FCSTD DOCUMENT  (FreeCAD 0.21R33771 (Git))
Label: RING3
License: All rights reserved
LicenseURL: http://en.wikipedia.org/wiki/All_rights_reserved
objects: Part::Part2DObjectPython×252, App::FeaturePython×24, App::DocumentObjectGroup×1
note: 252 computed .brp shape members not serialized (recipe doc carries the construction recipe); baked Part::Feature solids carry a one-line shape summary decoded from their .brp

FEATURE [Part::Part2DObjectPython] Rectangle  # Draft 2D object (typed FeaturePython)
  Area = 0
  ChamferSize = 0
  Columns = 1
  FilletRadius = 0
  Height = 6
  Length = 6
  MakeFace = false
  Placement = pos=(269.144,-43.1167,0) rot=(0,0,1;4.70122rad)
  Rows = 1
FEATURE [App::FeaturePython] Text  # WARN: FeaturePython — macro-defined, semantics opaque (R4)
  Placement = pos=(270.79,-53.3517,0) rot=(0,0,-1;4.73892rad)
  Text = 2
FEATURE [App::FeaturePython] Text001  # WARN: FeaturePython — macro-defined, semantics opaque (R4)
  Placement = pos=(268.047,49.5386,0) rot=(0,0,1;2.6241rad)
  Text = 6.
FEATURE [Part::Part2DObjectPython] Line  # Draft 2D object (typed FeaturePython)
  Area = 0
  ChamferSize = 0
  Closed = false
  End = (271.44,-106.146,0)
  FilletRadius = 0
  Length = 60
  MakeFace = true
  Placement = pos=(321.297,225.428,0) rot=(0,0,1;4.70122rad)
  Points = (2) [(272.11,-46.15,0),(332.11,-46.15,0)]
  Start = (272.11,-46.15,0)
  Subdivisions = 0
FEATURE [Part::Part2DObjectPython] Circle  # Draft 2D object (typed FeaturePython)
  Area = 1.13097
  FirstAngle = 0
  LastAngle = 0
  MakeFace = true
  Placement = pos=(272.07,-49.7498,0) rot=(0,0,1;4.70122rad)
  Radius = 0.6
FEATURE [Part::Part2DObjectPython] Rectangle001  # Draft 2D object (typed FeaturePython)
  Area = 0
  ChamferSize = 0
  Columns = 1
  FilletRadius = 0
  Height = 6
  Length = 6
  MakeFace = false
  Placement = pos=(270.385,-29.144,0) rot=(0,0,1;5.08397rad)
  Rows = 1
FEATURE [Part::Part2DObjectPython] Line001  # Draft 2D object (typed FeaturePython)
  Area = 0
  ChamferSize = 0
  Closed = false
  End = (296.055,-86.7553,0)
  FilletRadius = 0
  Length = 60
  MakeFace = true
  Placement = pos=(203.43,235.904,0) rot=(0,0,1;5.08397rad)
  Points = (2) [(274.27,-30.85,0),(334.27,-30.85,0)]
  Start = (274.27,-30.85,0)
  Subdivisions = 0
FEATURE [Part::Part2DObjectPython] Circle001  # Draft 2D object (typed FeaturePython)
  Area = 1.13097
  FirstAngle = 0
  LastAngle = 0
  MakeFace = true
  Placement = pos=(275.577,-34.2043,0) rot=(0,0,1;5.08397rad)
  Radius = 0.6
FEATURE [Part::Part2DObjectPython] Rectangle002  # Draft 2D object (typed FeaturePython)
  Area = 0
  ChamferSize = 0
  Columns = 1
  FilletRadius = 0
  Height = 6
  Length = 6
  MakeFace = false
  Placement = pos=(271.331,-15.2783,0) rot=(0,0,1;5.4573rad)
  Rows = 1
FEATURE [Part::Part2DObjectPython] Line002  # Draft 2D object (typed FeaturePython)
  Area = 0
  ChamferSize = 0
  Closed = false
  End = (316.244,-59.5591,0)
  FilletRadius = 0
  Length = 60
  MakeFace = true
  Placement = pos=(100.118,197.609,0) rot=(0,0,1;5.4573rad)
  Points = (2) [(275.57,-15.45,0),(335.57,-15.45,0)]
  Start = (275.57,-15.45,0)
  Subdivisions = 0
FEATURE [Part::Part2DObjectPython] Circle002  # Draft 2D object (typed FeaturePython)
  Area = 1.13097
  FirstAngle = 0
  LastAngle = 0
  MakeFace = true
  Placement = pos=(278.01,-18.0965,0) rot=(0,0,1;5.4573rad)
  Radius = 0.6
FEATURE [Part::Part2DObjectPython] Rectangle003  # Draft 2D object (typed FeaturePython)
  Area = 0
  ChamferSize = 0
  Columns = 1
  FilletRadius = 0
  Height = 6
  Length = 6
  MakeFace = false
  Placement = pos=(271.89,-1.0508,0) rot=(0,0,1;5.74807rad)
  Rows = 1
FEATURE [Part::Part2DObjectPython] Line003  # Draft 2D object (typed FeaturePython)
  Area = 0
  ChamferSize = 0
  Closed = false
  End = (327.613,-30.5966,0)
  FilletRadius = 0
  Length = 60
  MakeFace = true
  Placement = pos=(38.5825,140.744,0) rot=(0,0,1;5.74807rad)
  Points = (2) [(276,0,0),(336,0,0)]
  Start = (276,-5.68e-14,0)
  Subdivisions = 0
FEATURE [Part::Part2DObjectPython] Circle003  # Draft 2D object (typed FeaturePython)
  Area = 1.13097
  FirstAngle = 0
  LastAngle = 0
  MakeFace = true
  Placement = pos=(279.097,-1.83579,0) rot=(0,0,1;5.74807rad)
  Radius = 0.6
FEATURE [Part::Part2DObjectPython] Rectangle004  # Draft 2D object (typed FeaturePython)
  Area = 0
  ChamferSize = 0
  Columns = 1
  FilletRadius = 0
  Height = 6
  Length = 6
  MakeFace = false
  Placement = pos=(271.77,13.5629,0) rot=(0,0,1;5.95873rad)
  Rows = 1
FEATURE [Part::Part2DObjectPython] Line004  # Draft 2D object (typed FeaturePython)
  Area = 0
  ChamferSize = 0
  Closed = false
  End = (332.439,-3.67763,0)
  FilletRadius = 0
  Length = 60
  MakeFace = true
  Placement = pos=(9.45276,88.6561,0) rot=(0,0,1;5.95873rad)
  Points = (2) [(275.57,15.45,0),(335.57,15.45,0)]
  Start = (275.57,15.45,0)
  Subdivisions = 0
FEATURE [Part::Part2DObjectPython] Circle004  # Draft 2D object (typed FeaturePython)
  Area = 1.13097
  FirstAngle = 0
  LastAngle = 0
  MakeFace = true
  Placement = pos=(278.982,14.3023,0) rot=(0,0,1;5.95873rad)
  Radius = 0.6
FEATURE [Part::Part2DObjectPython] Rectangle005  # Draft 2D object (typed FeaturePython)
  Area = 0
  ChamferSize = 0
  Columns = 1
  FilletRadius = 0
  Height = 6
  Length = 6
  MakeFace = false
  Placement = pos=(270.817,28.3851,0) rot=(0,0,1;6.11773rad)
  Rows = 1
FEATURE [Part::Part2DObjectPython] Line005  # Draft 2D object (typed FeaturePython)
  Area = 0
  ChamferSize = 0
  Closed = false
  End = (333.451,20.9678,0)
  FilletRadius = 0
  Length = 60
  MakeFace = true
  Placement = pos=(-1.33543,45.5945,0) rot=(0,0,1;6.11773rad)
  Points = (2) [(274.27,30.85,0),(334.27,30.85,0)]
  Start = (274.27,30.85,0)
  Subdivisions = 0
FEATURE [Part::Part2DObjectPython] Circle005  # Draft 2D object (typed FeaturePython)
  Area = 1.13097
  FirstAngle = 0
  LastAngle = 0
  MakeFace = true
  Placement = pos=(277.821,30.2571,0) rot=(0,0,1;6.11773rad)
  Radius = 0.6
FEATURE [Part::Part2DObjectPython] Rectangle006  # Draft 2D object (typed FeaturePython)
  Area = 0
  ChamferSize = 0
  Columns = 1
  FilletRadius = 0
  Height = 6
  Length = 6
  MakeFace = false
  Placement = pos=(268.997,43.2674,0) rot=(0,0,1;6.24479rad)
  Rows = 1
FEATURE [Part::Part2DObjectPython] Line006  # Draft 2D object (typed FeaturePython)
  Area = 0
  ChamferSize = 0
  Closed = false
  End = (332.066,43.8467,0)
  FilletRadius = 0
  Length = 60
  MakeFace = true
  Placement = pos=(-1.57103,10.4797,0) rot=(0,0,1;6.24479rad)
  Points = (2) [(272.11,46.15,0),(332.11,46.15,0)]
  Start = (272.11,46.15,0)
  Subdivisions = 0
FEATURE [Part::Part2DObjectPython] Circle006  # Draft 2D object (typed FeaturePython)
  Area = 1.13097
  FirstAngle = 0
  LastAngle = 0
  MakeFace = true
  Placement = pos=(275.707,46.0118,0) rot=(0,0,1;6.24479rad)
  Radius = 0.6
FEATURE [Part::Part2DObjectPython] Rectangle007  # Draft 2D object (typed FeaturePython)
  Area = 0
  ChamferSize = 0
  Columns = 1
  FilletRadius = 0
  Height = 6
  Length = 6
  MakeFace = false
  Placement = pos=(256.356,92.5739,0) rot=(0,0,1;0.191463rad)
  Rows = 1
FEATURE [App::FeaturePython] Text002  # WARN: FeaturePython — macro-defined, semantics opaque (R4)
  Placement = pos=(261.188,89.1931,0) rot=(0,0,-1;4.21532rad)
  Text = 2
FEATURE [App::FeaturePython] Text003  # WARN: FeaturePython — macro-defined, semantics opaque (R4)
  Placement = pos=(207.363,176.926,0) rot=(0,0,1;3.1477rad)
  Text = 7
FEATURE [Part::Part2DObjectPython] Line007  # Draft 2D object (typed FeaturePython)
  Area = 0
  ChamferSize = 0
  Closed = false
  End = (317.634,107.508,0)
  FilletRadius = 0
  Length = 60
  MakeFace = true
  Placement = pos=(23.0132,-47.4792,0) rot=(0,0,1;0.191463rad)
  Points = (2) [(258.73,96.09,0),(318.73,96.09,0)]
  Start = (258.73,96.09,0)
  Subdivisions = 0
FEATURE [Part::Part2DObjectPython] Circle007  # Draft 2D object (typed FeaturePython)
  Area = 1.13097
  FirstAngle = 0
  LastAngle = 0
  MakeFace = true
  Placement = pos=(262.264,96.7751,0) rot=(0,0,1;0.191463rad)
  Radius = 0.6
FEATURE [Part::Part2DObjectPython] Rectangle008  # Draft 2D object (typed FeaturePython)
  Area = 0
  ChamferSize = 0
  Columns = 1
  FilletRadius = 0
  Height = 6
  Length = 6
  MakeFace = false
  Placement = pos=(250.416,107.017,0) rot=(0,0,1;0.145211rad)
  Rows = 1
FEATURE [Part::Part2DObjectPython] Line008  # Draft 2D object (typed FeaturePython)
  Area = 0
  ChamferSize = 0
  Closed = false
  End = (312.319,119.102,0)
  FilletRadius = 0
  Length = 60
  MakeFace = true
  Placement = pos=(18.6402,-35.4401,0) rot=(0,0,1;0.145211rad)
  Points = (2) [(252.95,110.42,0),(312.95,110.42,0)]
  Start = (252.95,110.42,0)
  Subdivisions = 0
FEATURE [Part::Part2DObjectPython] Circle008  # Draft 2D object (typed FeaturePython)
  Area = 1.13097
  FirstAngle = 0
  LastAngle = 0
  MakeFace = true
  Placement = pos=(256.512,110.941,0) rot=(0,0,1;0.145211rad)
  Radius = 0.6
FEATURE [Part::Part2DObjectPython] Rectangle009  # Draft 2D object (typed FeaturePython)
  Area = 0
  ChamferSize = 0
  Columns = 1
  FilletRadius = 0
  Height = 6
  Length = 6
  MakeFace = false
  Placement = pos=(243.301,121.481,0) rot=(0,0,1;6.2598rad)
  Rows = 1
FEATURE [Part::Part2DObjectPython] Line009  # Draft 2D object (typed FeaturePython)
  Area = 0
  ChamferSize = 0
  Closed = false
  End = (306.354,123.007,0)
  FilletRadius = 0
  Length = 60
  MakeFace = true
  Placement = pos=(-2.84199,5.79545,0) rot=(0,0,1;6.2598rad)
  Points = (2) [(246.37,124.41,0),(306.37,124.41,0)]
  Start = (246.37,124.41,0)
  Subdivisions = 0
FEATURE [Part::Part2DObjectPython] Circle009  # Draft 2D object (typed FeaturePython)
  Area = 1.13097
  FirstAngle = 0
  LastAngle = 0
  MakeFace = true
  Placement = pos=(249.969,124.326,0) rot=(0,0,1;6.2598rad)
  Radius = 0.6
FEATURE [Part::Part2DObjectPython] Rectangle010  # Draft 2D object (typed FeaturePython)
  Area = 0
  ChamferSize = 0
  Columns = 1
  FilletRadius = 0
  Height = 6
  Length = 6
  MakeFace = false
  Placement = pos=(235.214,136.126,0) rot=(0,0,1;5.95541rad)
  Rows = 1
FEATURE [Part::Part2DObjectPython] Line010  # Draft 2D object (typed FeaturePython)
  Area = 0
  ChamferSize = 0
  Closed = false
  End = (295.826,118.684,0)
  FilletRadius = 0
  Length = 60
  MakeFace = true
  Placement = pos=(-31.702,84.2958,0) rot=(0,0,1;5.95541rad)
  Points = (2) [(239.02,138,0),(299.02,138,0)]
  Start = (239.02,138,0)
  Subdivisions = 0
FEATURE [Part::Part2DObjectPython] Circle010  # Draft 2D object (typed FeaturePython)
  Area = 1.13097
  FirstAngle = 0
  LastAngle = 0
  MakeFace = true
  Placement = pos=(242.428,136.841,0) rot=(0,0,1;5.95541rad)
  Radius = 0.6
FEATURE [Part::Part2DObjectPython] Rectangle011  # Draft 2D object (typed FeaturePython)
  Area = 0
  ChamferSize = 0
  Columns = 1
  FilletRadius = 0
  Height = 6
  Length = 6
  MakeFace = false
  Placement = pos=(226.732,150.48,0) rot=(0,0,1;5.65871rad)
  Rows = 1
FEATURE [Part::Part2DObjectPython] Line011  # Draft 2D object (typed FeaturePython)
  Area = 0
  ChamferSize = 0
  Closed = false
  End = (279.596,116.08,0)
  FilletRadius = 0
  Length = 60
  MakeFace = true
  Placement = pos=(-44.7974,163.542,0) rot=(0,0,1;5.65871rad)
  Points = (2) [(230.92,151.16,0),(290.92,151.16,0)]
  Start = (230.92,151.16,0)
  Subdivisions = 0
FEATURE [Part::Part2DObjectPython] Circle011  # Draft 2D object (typed FeaturePython)
  Area = 1.13097
  FirstAngle = 0
  LastAngle = 0
  MakeFace = true
  Placement = pos=(233.841,149.055,0) rot=(0,0,1;5.65871rad)
  Radius = 0.6
FEATURE [Part::Part2DObjectPython] Rectangle012  # Draft 2D object (typed FeaturePython)
  Area = 0
  ChamferSize = 0
  Columns = 1
  FilletRadius = 0
  Height = 6
  Length = 6
  MakeFace = false
  Placement = pos=(217.857,163.826,0) rot=(0,0,1;5.50337rad)
  Rows = 1
FEATURE [Part::Part2DObjectPython] Line012  # Draft 2D object (typed FeaturePython)
  Area = 0
  ChamferSize = 0
  Closed = false
  End = (264.763,121.661,0)
  FilletRadius = 0
  Length = 60
  MakeFace = true
  Placement = pos=(-51.0336,203.514,0) rot=(0,0,1;5.50337rad)
  Points = (2) [(222.1,163.85,0),(282.1,163.85,0)]
  Start = (222.1,163.85,0)
  Subdivisions = 0
FEATURE [Part::Part2DObjectPython] Circle012  # Draft 2D object (typed FeaturePython)
  Area = 1.13097
  FirstAngle = 0
  LastAngle = 0
  MakeFace = true
  Placement = pos=(224.66,161.319,0) rot=(0,0,1;5.50337rad)
  Radius = 0.6
FEATURE [Part::Part2DObjectPython] Rectangle013  # Draft 2D object (typed FeaturePython)
  Area = 0
  ChamferSize = 0
  Columns = 1
  FilletRadius = 0
  Height = 6
  Length = 6
  MakeFace = false
  Placement = pos=(208.339,176.143,0) rot=(0,0,1;5.46882rad)
  Rows = 1
FEATURE [Part::Part2DObjectPython] Line013  # Draft 2D object (typed FeaturePython)
  Area = 0
  ChamferSize = 0
  Closed = false
  End = (253.76,132.382,0)
  FilletRadius = 0
  Length = 60
  MakeFace = true
  Placement = pos=(-61.3375,209.821,0) rot=(0,0,1;5.46882rad)
  Points = (2) [(212.58,176.02,0),(272.58,176.02,0)]
  Start = (212.58,176.02,0)
  Subdivisions = 0
FEATURE [Part::Part2DObjectPython] Circle013  # Draft 2D object (typed FeaturePython)
  Area = 1.13097
  FirstAngle = 0
  LastAngle = 0
  MakeFace = true
  Placement = pos=(215.051,173.402,0) rot=(0,0,1;5.46882rad)
  Radius = 0.6
FEATURE [Part::Part2DObjectPython] Rectangle014  # Draft 2D object (typed FeaturePython)
  Area = 0
  ChamferSize = 0
  Columns = 1
  FilletRadius = 0
  Height = 6
  Length = 6
  MakeFace = false
  Placement = pos=(171.868,211.706,0) rot=(0,0,1;5.70531rad)
  Rows = 1
FEATURE [App::FeaturePython] Text004  # WARN: FeaturePython — macro-defined, semantics opaque (R4)
  Placement = pos=(181.597,207.836,0) rot=(0,0,-1;3.69172rad)
  Text = 2
FEATURE [App::FeaturePython] Text005  # WARN: FeaturePython — macro-defined, semantics opaque (R4)
  Placement = pos=(91.1209,256.902,0) rot=(0,0,1;3.6713rad)
  Text = 8
FEATURE [Part::Part2DObjectPython] Line014  # Draft 2D object (typed FeaturePython)
  Area = 0
  ChamferSize = 0
  Closed = false
  End = (226.277,179.805,0)
  FilletRadius = 0
  Length = 60
  MakeFace = true
  Placement = pos=(-87.5399,130.669,0) rot=(0,0,1;5.70531rad)
  Points = (2) [(176.02,212.58,0),(236.02,212.58,0)]
  Start = (176.02,212.58,0)
  Subdivisions = 0
FEATURE [Part::Part2DObjectPython] Circle014  # Draft 2D object (typed FeaturePython)
  Area = 1.13097
  FirstAngle = 0
  LastAngle = 0
  MakeFace = true
  Placement = pos=(179.035,210.614,0) rot=(0,0,1;5.70531rad)
  Radius = 0.6
FEATURE [Part::Part2DObjectPython] Rectangle015  # Draft 2D object (typed FeaturePython)
  Area = 0
  ChamferSize = 0
  Columns = 1
  FilletRadius = 0
  Height = 6
  Length = 6
  MakeFace = false
  Placement = pos=(159.811,220.802,0) rot=(0,0,1;5.80863rad)
  Rows = 1
FEATURE [Part::Part2DObjectPython] Line015  # Draft 2D object (typed FeaturePython)
  Area = 0
  ChamferSize = 0
  Closed = false
  End = (217.22,194.683,0)
  FilletRadius = 0
  Length = 60
  MakeFace = true
  Placement = pos=(-83.3809,99.413,0) rot=(0,0,1;5.80863rad)
  Points = (2) [(163.85,222.1,0),(223.85,222.1,0)]
  Start = (163.85,222.1,0)
  Subdivisions = 0
FEATURE [Part::Part2DObjectPython] Circle015  # Draft 2D object (typed FeaturePython)
  Area = 1.13097
  FirstAngle = 0
  LastAngle = 0
  MakeFace = true
  Placement = pos=(167.052,220.455,0) rot=(0,0,1;5.80863rad)
  Radius = 0.6
FEATURE [Part::Part2DObjectPython] Rectangle016  # Draft 2D object (typed FeaturePython)
  Area = 0
  ChamferSize = 0
  Columns = 1
  FilletRadius = 0
  Height = 6
  Length = 6
  MakeFace = false
  Placement = pos=(147.277,229.211,0) rot=(0,0,1;5.91248rad)
  Rows = 1
FEATURE [Part::Part2DObjectPython] Line016  # Draft 2D object (typed FeaturePython)
  Area = 0
  ChamferSize = 0
  Closed = false
  End = (207.084,209.183,0)
  FilletRadius = 0
  Length = 60
  MakeFace = true
  Placement = pos=(-73.3885,70.4477,0) rot=(0,0,1;5.91248rad)
  Points = (2) [(151.16,230.92,0),(211.16,230.92,0)]
  Start = (151.16,230.92,0)
  Subdivisions = 0
FEATURE [Part::Part2DObjectPython] Circle016  # Draft 2D object (typed FeaturePython)
  Area = 1.13097
  FirstAngle = 0
  LastAngle = 0
  MakeFace = true
  Placement = pos=(154.515,229.616,0) rot=(0,0,1;5.91248rad)
  Radius = 0.6
FEATURE [Part::Part2DObjectPython] Rectangle017  # Draft 2D object (typed FeaturePython)
  Area = 0
  ChamferSize = 0
  Columns = 1
  FilletRadius = 0
  Height = 6
  Length = 6
  MakeFace = false
  Placement = pos=(134.314,236.919,0) rot=(0,0,1;6.0158rad)
  Rows = 1
FEATURE [Part::Part2DObjectPython] Line017  # Draft 2D object (typed FeaturePython)
  Area = 0
  ChamferSize = 0
  Closed = false
  End = (195.868,223.167,0)
  FilletRadius = 0
  Length = 60
  MakeFace = true
  Placement = pos=(-58.2476,44.9545,0) rot=(0,0,1;6.0158rad)
  Points = (2) [(138,239.02,0),(198,239.02,0)]
  Start = (138,239.02,0)
  Subdivisions = 0
FEATURE [Part::Part2DObjectPython] Circle017  # Draft 2D object (typed FeaturePython)
  Area = 1.13097
  FirstAngle = 0
  LastAngle = 0
  MakeFace = true
  Placement = pos=(141.472,238.069,0) rot=(0,0,1;6.0158rad)
  Radius = 0.6
FEATURE [Part::Part2DObjectPython] Rectangle018  # Draft 2D object (typed FeaturePython)
  Area = 0
  ChamferSize = 0
  Columns = 1
  FilletRadius = 0
  Height = 6
  Length = 6
  MakeFace = false
  Placement = pos=(120.961,243.9,0) rot=(0,0,1;6.1193rad)
  Rows = 1
FEATURE [Part::Part2DObjectPython] Line018  # Draft 2D object (typed FeaturePython)
  Area = 0
  ChamferSize = 0
  Closed = false
  End = (183.606,236.581,0)
  FilletRadius = 0
  Length = 60
  MakeFace = true
  Placement = pos=(-38.5292,23.5992,0) rot=(0,0,1;6.1193rad)
  Points = (2) [(124.41,246.37,0),(184.41,246.37,0)]
  Start = (124.41,246.37,0)
  Subdivisions = 0
FEATURE [Part::Part2DObjectPython] Circle018  # Draft 2D object (typed FeaturePython)
  Area = 1.13097
  FirstAngle = 0
  LastAngle = 0
  MakeFace = true
  Placement = pos=(127.962,245.783,0) rot=(0,0,1;6.1193rad)
  Radius = 0.6
FEATURE [Part::Part2DObjectPython] Rectangle019  # Draft 2D object (typed FeaturePython)
  Area = 0
  ChamferSize = 0
  Columns = 1
  FilletRadius = 0
  Height = 6
  Length = 6
  MakeFace = false
  Placement = pos=(107.269,250.109,0) rot=(0,0,1;6.23152rad)
  Rows = 1
FEATURE [Part::Part2DObjectPython] Line019  # Draft 2D object (typed FeaturePython)
  Area = 0
  ChamferSize = 0
  Closed = false
  End = (170.34,249.852,0)
  FilletRadius = 0
  Length = 60
  MakeFace = true
  Placement = pos=(-12.9147,6.03943,0) rot=(0,0,1;6.23152rad)
  Points = (2) [(110.42,252.95,0),(170.42,252.95,0)]
  Start = (110.42,252.95,0)
  Subdivisions = 0
FEATURE [Part::Part2DObjectPython] Circle019  # Draft 2D object (typed FeaturePython)
  Area = 1.13097
  FirstAngle = 0
  LastAngle = 0
  MakeFace = true
  Placement = pos=(114.015,252.764,0) rot=(0,0,1;6.23152rad)
  Radius = 0.6
FEATURE [Part::Part2DObjectPython] Rectangle020  # Draft 2D object (typed FeaturePython)
  Area = 0
  ChamferSize = 0
  Columns = 1
  FilletRadius = 0
  Height = 6
  Length = 6
  MakeFace = false
  Placement = pos=(93.3516,255.489,0) rot=(0,0,1;0.083776rad)
  Rows = 1
FEATURE [Part::Part2DObjectPython] Line020  # Draft 2D object (typed FeaturePython)
  Area = 0
  ChamferSize = 0
  Closed = false
  End = (155.88,263.751,0)
  FilletRadius = 0
  Length = 60
  MakeFace = true
  Placement = pos=(21.987,-7.1332,0) rot=(0,0,1;0.083776rad)
  Points = (2) [(96.09,258.73,0),(156.09,258.73,0)]
  Start = (96.09,258.73,0)
  Subdivisions = 0
FEATURE [Part::Part2DObjectPython] Circle020  # Draft 2D object (typed FeaturePython)
  Area = 1.13097
  FirstAngle = 0
  LastAngle = 0
  MakeFace = true
  Placement = pos=(99.6774,259.031,0) rot=(0,0,1;0.083776rad)
  Radius = 0.6
FEATURE [Part::Part2DObjectPython] Rectangle021  # Draft 2D object (typed FeaturePython)
  Area = 0
  ChamferSize = 0
  Columns = 1
  FilletRadius = 0
  Height = 6
  Length = 6
  MakeFace = false
  Placement = pos=(48.0649,268.324,0) rot=(0,0,1;1.25367rad)
  Rows = 1
FEATURE [App::FeaturePython] Text006  # WARN: FeaturePython — macro-defined, semantics opaque (R4)
  Placement = pos=(53.3517,270.79,0) rot=(0,0,-1;3.16812rad)
  Text = 2
FEATURE [App::FeaturePython] Text007  # WARN: FeaturePython — macro-defined, semantics opaque (R4)
  Placement = pos=(-49.5386,268.047,0) rot=(0,0,1;4.1949rad)
  Text = 9
FEATURE [Part::Part2DObjectPython] Line021  # Draft 2D object (typed FeaturePython)
  Area = 0
  ChamferSize = 0
  Closed = false
  End = (64.8602,329.118,0)
  FilletRadius = 0
  Length = 60
  MakeFace = true
  Placement = pos=(290.3,143.407,0) rot=(0,0,1;1.25367rad)
  Points = (2) [(46.15,272.11,0),(106.15,272.11,0)]
  Start = (46.15,272.11,0)
  Subdivisions = 0
FEATURE [Part::Part2DObjectPython] Circle021  # Draft 2D object (typed FeaturePython)
  Area = 1.13097
  FirstAngle = 0
  LastAngle = 0
  MakeFace = true
  Placement = pos=(47.2726,275.53,0) rot=(0,0,1;1.25367rad)
  Radius = 0.6
FEATURE [Part::Part2DObjectPython] Rectangle022  # Draft 2D object (typed FeaturePython)
  Area = 0
  ChamferSize = 0
  Columns = 1
  FilletRadius = 0
  Height = 6
  Length = 6
  MakeFace = false
  Placement = pos=(34.7405,272.578,0) rot=(0,0,1;1.94587rad)
  Rows = 1
FEATURE [Part::Part2DObjectPython] Line022  # Draft 2D object (typed FeaturePython)
  Area = 0
  ChamferSize = 0
  Closed = false
  End = (8.86967,330.099,0)
  FilletRadius = 0
  Length = 60
  MakeFace = true
  Placement = pos=(297.355,346.04,0) rot=(0,0,1;1.94587rad)
  Points = (2) [(30.85,274.27,0),(90.85,274.27,0)]
  Start = (30.85,274.27,0)
  Subdivisions = 0
FEATURE [Part::Part2DObjectPython] Circle022  # Draft 2D object (typed FeaturePython)
  Area = 1.13097
  FirstAngle = 0
  LastAngle = 0
  MakeFace = true
  Placement = pos=(29.5312,277.62,0) rot=(0,0,1;1.94587rad)
  Radius = 0.6
FEATURE [Part::Part2DObjectPython] Rectangle023  # Draft 2D object (typed FeaturePython)
  Area = 0
  ChamferSize = 0
  Columns = 1
  FilletRadius = 0
  Height = 6
  Length = 6
  MakeFace = false
  Placement = pos=(19.6498,276.171,0) rot=(0,0,1;2.49844rad)
  Rows = 1
FEATURE [Part::Part2DObjectPython] Line023  # Draft 2D object (typed FeaturePython)
  Area = 0
  ChamferSize = 0
  Closed = false
  End = (-32.5625,311.553,0)
  FilletRadius = 0
  Length = 60
  MakeFace = true
  Placement = pos=(193.079,486.818,0) rot=(0,0,1;2.49844rad)
  Points = (2) [(15.45,275.57,0),(75.45,275.57,0)]
  Start = (15.45,275.57,0)
  Subdivisions = 0
FEATURE [Part::Part2DObjectPython] Circle023  # Draft 2D object (typed FeaturePython)
  Area = 1.13097
  FirstAngle = 0
  LastAngle = 0
  MakeFace = true
  Placement = pos=(12.5693,277.729,0) rot=(0,0,1;2.49844rad)
  Radius = 0.6
FEATURE [Part::Part2DObjectPython] Rectangle024  # Draft 2D object (typed FeaturePython)
  Area = 0
  ChamferSize = 0
  Columns = 1
  FilletRadius = 0
  Height = 6
  Length = 6
  MakeFace = false
  Placement = pos=(3.67238,278.125,0) rot=(0,0,1;2.88067rad)
  Rows = 1
FEATURE [Part::Part2DObjectPython] Line024  # Draft 2D object (typed FeaturePython)
  Area = 0
  ChamferSize = 0
  Closed = false
  End = (-57.9691,291.479,0)
  FilletRadius = 0
  Length = 60
  MakeFace = true
  Placement = pos=(71.2014,542.658,0) rot=(0,0,1;2.88067rad)
  Points = (2) [(0,276,0),(60,276,0)]
  Start = (0,276,0)
  Subdivisions = 0
FEATURE [Part::Part2DObjectPython] Circle024  # Draft 2D object (typed FeaturePython)
  Area = 1.13097
  FirstAngle = 0
  LastAngle = 0
  MakeFace = true
  Placement = pos=(-3.47814,276.929,0) rot=(0,0,1;2.88067rad)
  Radius = 0.6
FEATURE [Part::Part2DObjectPython] Rectangle025  # Draft 2D object (typed FeaturePython)
  Area = 0
  ChamferSize = 0
  Columns = 1
  FilletRadius = 0
  Height = 6
  Length = 6
  MakeFace = false
  Placement = pos=(-12.4484,278.568,0) rot=(0,0,1;3.14107rad)
  Rows = 1
FEATURE [Part::Part2DObjectPython] Line025  # Draft 2D object (typed FeaturePython)
  Area = 0
  ChamferSize = 0
  Closed = false
  End = (-75.45,275.601,0)
  FilletRadius = 0
  Length = 60
  MakeFace = true
  Placement = pos=(-30.7557,551.148,0) rot=(0,0,1;3.14107rad)
  Points = (2) [(-15.45,275.57,0),(44.55,275.57,0)]
  Start = (-15.45,275.57,0)
  Subdivisions = 0
FEATURE [Part::Part2DObjectPython] Circle025  # Draft 2D object (typed FeaturePython)
  Area = 1.13097
  FirstAngle = 0
  LastAngle = 0
  MakeFace = true
  Placement = pos=(-19.05,275.572,0) rot=(0,0,1;3.14107rad)
  Radius = 0.6
FEATURE [Part::Part2DObjectPython] Rectangle026  # Draft 2D object (typed FeaturePython)
  Area = 0
  ChamferSize = 0
  Columns = 1
  FilletRadius = 0
  Height = 6
  Length = 6
  MakeFace = false
  Placement = pos=(-27.849,277.269,0) rot=(0,0,1;3.14124rad)
  Rows = 1
FEATURE [Part::Part2DObjectPython] Line026  # Draft 2D object (typed FeaturePython)
  Area = 0
  ChamferSize = 0
  Closed = false
  End = (-90.85,274.291,0)
  FilletRadius = 0
  Length = 60
  MakeFace = true
  Placement = pos=(-61.6043,548.551,0) rot=(0,0,1;3.14124rad)
  Points = (2) [(-30.85,274.27,0),(29.15,274.27,0)]
  Start = (-30.85,274.27,0)
  Subdivisions = 0
FEATURE [Part::Part2DObjectPython] Circle026  # Draft 2D object (typed FeaturePython)
  Area = 1.13097
  FirstAngle = 0
  LastAngle = 0
  MakeFace = true
  Placement = pos=(-34.45,274.271,0) rot=(0,0,1;3.14124rad)
  Radius = 0.6
FEATURE [Part::Part2DObjectPython] Rectangle027  # Draft 2D object (typed FeaturePython)
  Area = 0
  ChamferSize = 0
  Columns = 1
  FilletRadius = 0
  Height = 6
  Length = 6
  MakeFace = false
  Placement = pos=(-43.15,275.11,0) rot=(0,0,1;3.14159rad)
  Rows = 1
FEATURE [Part::Part2DObjectPython] Line027  # Draft 2D object (typed FeaturePython)
  Area = 0
  ChamferSize = 0
  Closed = false
  End = (-106.15,272.11,0)
  FilletRadius = 0
  Length = 60
  MakeFace = true
  Placement = pos=(-92.3,544.22,0) rot=(0,0,1;3.14159rad)
  Points = (2) [(-46.15,272.11,0),(13.85,272.11,0)]
  Start = (-46.15,272.11,0)
  Subdivisions = 0
FEATURE [Part::Part2DObjectPython] Circle027  # Draft 2D object (typed FeaturePython)
  Area = 1.13097
  FirstAngle = 0
  LastAngle = 0
  MakeFace = true
  Placement = pos=(-49.75,272.11,0) rot=(0,0,1;3.14159rad)
  Radius = 0.6
FEATURE [Part::Part2DObjectPython] Rectangle028  # Draft 2D object (typed FeaturePython)
  Area = 0
  ChamferSize = 0
  Columns = 1
  FilletRadius = 0
  Height = 6
  Length = 6
  MakeFace = false
  Placement = pos=(-93.09,261.73,0) rot=(0,0,1;3.14159rad)
  Rows = 1
FEATURE [App::FeaturePython] Text008  # WARN: FeaturePython — macro-defined, semantics opaque (R4)
  Placement = pos=(-89.1931,261.188,0) rot=(0,0,-1;2.64452rad)
  Text = 2
FEATURE [App::FeaturePython] Text009  # WARN: FeaturePython — macro-defined, semantics opaque (R4)
  Placement = pos=(-176.926,207.363,0) rot=(0,0,1;4.7185rad)
  Text = 10
FEATURE [Part::Part2DObjectPython] Line028  # Draft 2D object (typed FeaturePython)
  Area = 0
  ChamferSize = 0
  Closed = false
  End = (-156.09,258.73,0)
  FilletRadius = 0
  Length = 60
  MakeFace = true
  Placement = pos=(-192.18,517.46,0) rot=(0,0,1;3.14159rad)
  Points = (2) [(-96.09,258.73,0),(-36.09,258.73,0)]
  Start = (-96.09,258.73,0)
  Subdivisions = 0
FEATURE [Part::Part2DObjectPython] Circle028  # Draft 2D object (typed FeaturePython)
  Area = 1.13097
  FirstAngle = 0
  LastAngle = 0
  MakeFace = true
  Placement = pos=(-99.69,258.73,0) rot=(0,0,1;3.14159rad)
  Radius = 0.6
FEATURE [Part::Part2DObjectPython] Rectangle029  # Draft 2D object (typed FeaturePython)
  Area = 0
  ChamferSize = 0
  Columns = 1
  FilletRadius = 0
  Height = 6
  Length = 6
  MakeFace = false
  Placement = pos=(-107.42,255.95,0) rot=(0,0,1;3.14159rad)
  Rows = 1
FEATURE [Part::Part2DObjectPython] Line029  # Draft 2D object (typed FeaturePython)
  Area = 0
  ChamferSize = 0
  Closed = false
  End = (-170.42,252.95,0)
  FilletRadius = 0
  Length = 60
  MakeFace = true
  Placement = pos=(-220.84,505.9,0) rot=(0,0,1;3.14159rad)
  Points = (2) [(-110.42,252.95,0),(-50.42,252.95,0)]
  Start = (-110.42,252.95,0)
  Subdivisions = 0
FEATURE [Part::Part2DObjectPython] Circle029  # Draft 2D object (typed FeaturePython)
  Area = 1.13097
  FirstAngle = 0
  LastAngle = 0
  MakeFace = true
  Placement = pos=(-114.02,252.95,0) rot=(0,0,1;3.14159rad)
  Radius = 0.6
FEATURE [Part::Part2DObjectPython] Rectangle030  # Draft 2D object (typed FeaturePython)
  Area = 0
  ChamferSize = 0
  Columns = 1
  FilletRadius = 0
  Height = 6
  Length = 6
  MakeFace = false
  Placement = pos=(-125.426,250.489,0) rot=(0,0,1;4.16889rad)
  Rows = 1
FEATURE [Part::Part2DObjectPython] Line030  # Draft 2D object (typed FeaturePython)
  Area = 0
  ChamferSize = 0
  Closed = false
  End = (-155.438,195.016,0)
  FilletRadius = 0
  Length = 60
  MakeFace = true
  Placement = pos=(-399.616,267.292,0) rot=(0,0,1;4.16889rad)
  Points = (2) [(-124.41,246.37,0),(-64.41,246.37,0)]
  Start = (-124.41,246.37,0)
  Subdivisions = 0
FEATURE [Part::Part2DObjectPython] Circle030  # Draft 2D object (typed FeaturePython)
  Area = 1.13097
  FirstAngle = 0
  LastAngle = 0
  MakeFace = true
  Placement = pos=(-126.272,243.289,0) rot=(0,0,1;4.16889rad)
  Radius = 0.6
FEATURE [Part::Part2DObjectPython] Rectangle031  # Draft 2D object (typed FeaturePython)
  Area = 0
  ChamferSize = 0
  Columns = 1
  FilletRadius = 0
  Height = 6
  Length = 6
  MakeFace = false
  Placement = pos=(-138.447,243.239,0) rot=(0,0,1;4.03258rad)
  Rows = 1
FEATURE [Part::Part2DObjectPython] Line031  # Draft 2D object (typed FeaturePython)
  Area = 0
  ChamferSize = 0
  Closed = false
  End = (-175.719,192.358,0)
  FilletRadius = 0
  Length = 60
  MakeFace = true
  Placement = pos=(-410.637,281.956,0) rot=(0,0,1;4.03258rad)
  Points = (2) [(-138,239.02,0),(-78,239.02,0)]
  Start = (-138,239.02,0)
  Subdivisions = 0
FEATURE [Part::Part2DObjectPython] Circle031  # Draft 2D object (typed FeaturePython)
  Area = 1.13097
  FirstAngle = 0
  LastAngle = 0
  MakeFace = true
  Placement = pos=(-140.263,236.22,0) rot=(0,0,1;4.03258rad)
  Radius = 0.6
FEATURE [Part::Part2DObjectPython] Rectangle032  # Draft 2D object (typed FeaturePython)
  Area = 0
  ChamferSize = 0
  Columns = 1
  FilletRadius = 0
  Height = 6
  Length = 6
  MakeFace = false
  Placement = pos=(-148.16,233.92,0) rot=(0,0,1;3.14159rad)
  Rows = 1
FEATURE [Part::Part2DObjectPython] Line032  # Draft 2D object (typed FeaturePython)
  Area = 0
  ChamferSize = 0
  Closed = false
  End = (-211.16,230.92,0)
  FilletRadius = 0
  Length = 60
  MakeFace = true
  Placement = pos=(-302.32,461.84,0) rot=(0,0,1;3.14159rad)
  Points = (2) [(-151.16,230.92,0),(-91.16,230.92,0)]
  Start = (-151.16,230.92,0)
  Subdivisions = 0
FEATURE [Part::Part2DObjectPython] Circle032  # Draft 2D object (typed FeaturePython)
  Area = 1.13097
  FirstAngle = 0
  LastAngle = 0
  MakeFace = true
  Placement = pos=(-154.76,230.92,0) rot=(0,0,1;3.14159rad)
  Radius = 0.6
FEATURE [Part::Part2DObjectPython] Rectangle033  # Draft 2D object (typed FeaturePython)
  Area = 0
  ChamferSize = 0
  Columns = 1
  FilletRadius = 0
  Height = 6
  Length = 6
  MakeFace = false
  Placement = pos=(-161.861,225.847,0) rot=(0,0,1;3.439rad)
  Rows = 1
FEATURE [Part::Part2DObjectPython] Line033  # Draft 2D object (typed FeaturePython)
  Area = 0
  ChamferSize = 0
  Closed = false
  End = (-221.216,204.518,0)
  FilletRadius = 0
  Length = 60
  MakeFace = true
  Placement = pos=(-385.591,386.435,0) rot=(0,0,1;3.439rad)
  Points = (2) [(-163.85,222.1,0),(-103.85,222.1,0)]
  Start = (-163.85,222.1,0)
  Subdivisions = 0
FEATURE [Part::Part2DObjectPython] Circle033  # Draft 2D object (typed FeaturePython)
  Area = 1.13097
  FirstAngle = 0
  LastAngle = 0
  MakeFace = true
  Placement = pos=(-167.292,221.045,0) rot=(0,0,1;3.439rad)
  Radius = 0.6
FEATURE [Part::Part2DObjectPython] Rectangle034  # Draft 2D object (typed FeaturePython)
  Area = 0
  ChamferSize = 0
  Columns = 1
  FilletRadius = 0
  Height = 6
  Length = 6
  MakeFace = false
  Placement = pos=(-173.325,215.857,0) rot=(0,0,1;3.23863rad)
  Rows = 1
FEATURE [Part::Part2DObjectPython] Line034  # Draft 2D object (typed FeaturePython)
  Area = 0
  ChamferSize = 0
  Closed = false
  End = (-235.738,206.767,0)
  FilletRadius = 0
  Length = 60
  MakeFace = true
  Placement = pos=(-371.808,407.106,0) rot=(0,0,1;3.23863rad)
  Points = (2) [(-176.02,212.58,0),(-116.02,212.58,0)]
  Start = (-176.02,212.58,0)
  Subdivisions = 0
FEATURE [Part::Part2DObjectPython] Circle034  # Draft 2D object (typed FeaturePython)
  Area = 1.13097
  FirstAngle = 0
  LastAngle = 0
  MakeFace = true
  Placement = pos=(-179.603,212.231,0) rot=(0,0,1;3.23863rad)
  Radius = 0.6
FEATURE [Part::Part2DObjectPython] Rectangle035  # Draft 2D object (typed FeaturePython)
  Area = 0
  ChamferSize = 0
  Columns = 1
  FilletRadius = 0
  Height = 6
  Length = 6
  MakeFace = false
  Placement = pos=(-209.548,178.988,0) rot=(0,0,1;3.13095rad)
  Rows = 1
FEATURE [App::FeaturePython] Text010  # WARN: FeaturePython — macro-defined, semantics opaque (R4)
  Placement = pos=(-207.836,181.597,0) rot=(0,0,-1;2.12092rad)
  Text = 2
FEATURE [App::FeaturePython] Text011  # WARN: FeaturePython — macro-defined, semantics opaque (R4)
  Placement = pos=(-256.902,91.1209,0) rot=(0,0,1;5.2421rad)
  Text = 11
FEATURE [Part::Part2DObjectPython] Line035  # Draft 2D object (typed FeaturePython)
  Area = 0
  ChamferSize = 0
  Closed = false
  End = (-272.577,176.659,0)
  FilletRadius = 0
  Length = 60
  MakeFace = true
  Placement = pos=(-423.274,354.293,0) rot=(0,0,1;3.13095rad)
  Points = (2) [(-212.58,176.02,0),(-152.58,176.02,0)]
  Start = (-212.58,176.02,0)
  Subdivisions = 0
FEATURE [Part::Part2DObjectPython] Circle035  # Draft 2D object (typed FeaturePython)
  Area = 1.13097
  FirstAngle = 0
  LastAngle = 0
  MakeFace = true
  Placement = pos=(-216.18,176.058,0) rot=(0,0,1;3.13095rad)
  Radius = 0.6
FEATURE [Part::Part2DObjectPython] Rectangle036  # Draft 2D object (typed FeaturePython)
  Area = 0
  ChamferSize = 0
  Columns = 1
  FilletRadius = 0
  Height = 6
  Length = 6
  MakeFace = false
  Placement = pos=(-219.095,166.845,0) rot=(0,0,1;3.14002rad)
  Rows = 1
FEATURE [Part::Part2DObjectPython] Line036  # Draft 2D object (typed FeaturePython)
  Area = 0
  ChamferSize = 0
  Closed = false
  End = (-282.1,163.944,0)
  FilletRadius = 0
  Length = 60
  MakeFace = true
  Placement = pos=(-443.942,328.049,0) rot=(0,0,1;3.14002rad)
  Points = (2) [(-222.1,163.85,0),(-162.1,163.85,0)]
  Start = (-222.1,163.85,0)
  Subdivisions = 0
FEATURE [Part::Part2DObjectPython] Circle036  # Draft 2D object (typed FeaturePython)
  Area = 1.13097
  FirstAngle = 0
  LastAngle = 0
  MakeFace = true
  Placement = pos=(-225.7,163.856,0) rot=(0,0,1;3.14002rad)
  Radius = 0.6
FEATURE [Part::Part2DObjectPython] Rectangle037  # Draft 2D object (typed FeaturePython)
  Area = 0
  ChamferSize = 0
  Columns = 1
  FilletRadius = 0
  Height = 6
  Length = 6
  MakeFace = false
  Placement = pos=(-228.336,154.525,0) rot=(0,0,1;3.27214rad)
  Rows = 1
FEATURE [Part::Part2DObjectPython] Line037  # Draft 2D object (typed FeaturePython)
  Area = 0
  ChamferSize = 0
  Closed = false
  End = (-290.409,143.349,0)
  FilletRadius = 0
  Length = 60
  MakeFace = true
  Placement = pos=(-479.553,270.972,0) rot=(0,0,1;3.27214rad)
  Points = (2) [(-230.92,151.16,0),(-170.92,151.16,0)]
  Start = (-230.92,151.16,0)
  Subdivisions = 0
FEATURE [Part::Part2DObjectPython] Circle037  # Draft 2D object (typed FeaturePython)
  Area = 1.13097
  FirstAngle = 0
  LastAngle = 0
  MakeFace = true
  Placement = pos=(-234.489,150.691,0) rot=(0,0,1;3.27214rad)
  Radius = 0.6
FEATURE [Part::Part2DObjectPython] Rectangle038  # Draft 2D object (typed FeaturePython)
  Area = 0
  ChamferSize = 0
  Columns = 1
  FilletRadius = 0
  Height = 6
  Length = 6
  MakeFace = false
  Placement = pos=(-236.588,141.476,0) rot=(0,0,1;3.31648rad)
  Rows = 1
FEATURE [Part::Part2DObjectPython] Line038  # Draft 2D object (typed FeaturePython)
  Area = 0
  ChamferSize = 0
  Closed = false
  End = (-298.105,127.56,0)
  FilletRadius = 0
  Length = 60
  MakeFace = true
  Placement = pos=(-498.405,232.308,0) rot=(0,0,1;3.31648rad)
  Points = (2) [(-239.02,138,0),(-179.02,138,0)]
  Start = (-239.02,138,0)
  Subdivisions = 0
FEATURE [Part::Part2DObjectPython] Circle038  # Draft 2D object (typed FeaturePython)
  Area = 1.13097
  FirstAngle = 0
  LastAngle = 0
  MakeFace = true
  Placement = pos=(-242.565,137.374,0) rot=(0,0,1;3.31648rad)
  Radius = 0.6
FEATURE [Part::Part2DObjectPython] Rectangle039  # Draft 2D object (typed FeaturePython)
  Area = 0
  ChamferSize = 0
  Columns = 1
  FilletRadius = 0
  Height = 6
  Length = 6
  MakeFace = false
  Placement = pos=(-244.059,127.968,0) rot=(0,0,1;3.35086rad)
  Rows = 1
FEATURE [Part::Part2DObjectPython] Line039  # Draft 2D object (typed FeaturePython)
  Area = 0
  ChamferSize = 0
  Closed = false
  End = (-305.061,111.946,0)
  FilletRadius = 0
  Length = 60
  MakeFace = true
  Placement = pos=(-513.21,194.925,0) rot=(0,0,1;3.35086rad)
  Points = (2) [(-246.37,124.41,0),(-186.37,124.41,0)]
  Start = (-246.37,124.41,0)
  Subdivisions = 0
FEATURE [Part::Part2DObjectPython] Circle039  # Draft 2D object (typed FeaturePython)
  Area = 1.13097
  FirstAngle = 0
  LastAngle = 0
  MakeFace = true
  Placement = pos=(-249.891,123.662,0) rot=(0,0,1;3.35086rad)
  Radius = 0.6
FEATURE [Part::Part2DObjectPython] Rectangle040  # Draft 2D object (typed FeaturePython)
  Area = 0
  ChamferSize = 0
  Columns = 1
  FilletRadius = 0
  Height = 6
  Length = 6
  MakeFace = false
  Placement = pos=(-250.711,114.024,0) rot=(0,0,1;3.3711rad)
  Rows = 1
FEATURE [Part::Part2DObjectPython] Line040  # Draft 2D object (typed FeaturePython)
  Area = 0
  ChamferSize = 0
  Closed = false
  End = (-311.377,96.7699,0)
  FilletRadius = 0
  Length = 60
  MakeFace = true
  Placement = pos=(-524.388,160.398,0) rot=(0,0,1;3.3711rad)
  Points = (2) [(-252.95,110.42,0),(-192.95,110.42,0)]
  Start = (-252.95,110.42,0)
  Subdivisions = 0
FEATURE [Part::Part2DObjectPython] Circle040  # Draft 2D object (typed FeaturePython)
  Area = 1.13097
  FirstAngle = 0
  LastAngle = 0
  MakeFace = true
  Placement = pos=(-256.456,109.601,0) rot=(0,0,1;3.3711rad)
  Radius = 0.6
FEATURE [Part::Part2DObjectPython] Rectangle041  # Draft 2D object (typed FeaturePython)
  Area = 0
  ChamferSize = 0
  Columns = 1
  FilletRadius = 0
  Height = 6
  Length = 6
  MakeFace = false
  Placement = pos=(-256.482,99.6884,0) rot=(0,0,1;3.36866rad)
  Rows = 1
FEATURE [Part::Part2DObjectPython] Line041  # Draft 2D object (typed FeaturePython)
  Area = 0
  ChamferSize = 0
  Closed = false
  End = (-317.19,82.5827,0)
  FilletRadius = 0
  Length = 60
  MakeFace = true
  Placement = pos=(-532.45,131.468,0) rot=(0,0,1;3.36866rad)
  Points = (2) [(-258.73,96.09,0),(-198.73,96.09,0)]
  Start = (-258.73,96.09,0)
  Subdivisions = 0
FEATURE [Part::Part2DObjectPython] Circle041  # Draft 2D object (typed FeaturePython)
  Area = 1.13097
  FirstAngle = 0
  LastAngle = 0
  MakeFace = true
  Placement = pos=(-262.238,95.2796,0) rot=(0,0,1;3.36866rad)
  Radius = 0.6
FEATURE [Part::Part2DObjectPython] Rectangle042  # Draft 2D object (typed FeaturePython)
  Area = 0
  ChamferSize = 0
  Columns = 1
  FilletRadius = 0
  Height = 6
  Length = 6
  MakeFace = false
  Placement = pos=(-269.081,49.1211,0) rot=(0,0,1;3.13199rad)
  Rows = 1
FEATURE [App::FeaturePython] Text012  # WARN: FeaturePython — macro-defined, semantics opaque (R4)
  Placement = pos=(-270.79,53.3517,0) rot=(0,0,-1;1.59733rad)
  Text = 2
FEATURE [App::FeaturePython] Text013  # WARN: FeaturePython — macro-defined, semantics opaque (R4)
  Placement = pos=(-268.047,-49.5386,0) rot=(0,0,1;5.7657rad)
  Text = 12
FEATURE [Part::Part2DObjectPython] Line042  # Draft 2D object (typed FeaturePython)
  Area = 0
  ChamferSize = 0
  Closed = false
  End = (-332.107,46.7259,0)
  FilletRadius = 0
  Length = 60
  MakeFace = true
  Placement = pos=(-543.764,94.9099,0) rot=(0,0,1;3.13199rad)
  Points = (2) [(-272.11,46.15,0),(-212.11,46.15,0)]
  Start = (-272.11,46.15,0)
  Subdivisions = 0
FEATURE [Part::Part2DObjectPython] Circle042  # Draft 2D object (typed FeaturePython)
  Area = 1.13097
  FirstAngle = 0
  LastAngle = 0
  MakeFace = true
  Placement = pos=(-275.71,46.1846,0) rot=(0,0,1;3.13199rad)
  Radius = 0.6
FEATURE [Part::Part2DObjectPython] Rectangle043  # Draft 2D object (typed FeaturePython)
  Area = 0
  ChamferSize = 0
  Columns = 1
  FilletRadius = 0
  Height = 6
  Length = 6
  MakeFace = false
  Placement = pos=(-271.382,33.9584,0) rot=(0,0,1;3.17842rad)
  Rows = 1
FEATURE [Part::Part2DObjectPython] Line043  # Draft 2D object (typed FeaturePython)
  Area = 0
  ChamferSize = 0
  Closed = false
  End = (-334.229,28.6409,0)
  FilletRadius = 0
  Length = 60
  MakeFace = true
  Placement = pos=(-549.49,51.581,0) rot=(0,0,1;3.17842rad)
  Points = (2) [(-274.27,30.85,0),(-214.27,30.85,0)]
  Start = (-274.27,30.85,0)
  Subdivisions = 0
FEATURE [Part::Part2DObjectPython] Circle043  # Draft 2D object (typed FeaturePython)
  Area = 1.13097
  FirstAngle = 0
  LastAngle = 0
  MakeFace = true
  Placement = pos=(-277.868,30.7175,0) rot=(0,0,1;3.17842rad)
  Radius = 0.6
FEATURE [Part::Part2DObjectPython] Rectangle044  # Draft 2D object (typed FeaturePython)
  Area = 0
  ChamferSize = 0
  Columns = 1
  FilletRadius = 0
  Height = 6
  Length = 6
  MakeFace = false
  Placement = pos=(-272.32,18.1771,0) rot=(0,0,1;3.05433rad)
  Rows = 1
FEATURE [Part::Part2DObjectPython] Line044  # Draft 2D object (typed FeaturePython)
  Area = 0
  ChamferSize = 0
  Closed = false
  End = (-335.342,20.6793,0)
  FilletRadius = 0
  Length = 60
  MakeFace = true
  Placement = pos=(-548.745,54.8587,0) rot=(0,0,1;3.05433rad)
  Points = (2) [(-275.57,15.45,0),(-215.57,15.45,0)]
  Start = (-275.57,15.45,0)
  Subdivisions = 0
FEATURE [Part::Part2DObjectPython] Circle044  # Draft 2D object (typed FeaturePython)
  Area = 1.13097
  FirstAngle = 0
  LastAngle = 0
  MakeFace = true
  Placement = pos=(-279.156,15.7638,0) rot=(0,0,1;3.05433rad)
  Radius = 0.6
FEATURE [Part::Part2DObjectPython] Rectangle045  # Draft 2D object (typed FeaturePython)
  Area = 0
  ChamferSize = 0
  Columns = 1
  FilletRadius = 0
  Height = 6
  Length = 6
  MakeFace = false
  Placement = pos=(-279.273,2.69922,0) rot=(0,0,1;4.80821rad)
  Rows = 1
FEATURE [Part::Part2DObjectPython] Line045  # Draft 2D object (typed FeaturePython)
  Area = 0
  ChamferSize = 0
  Closed = false
  End = (-270.26,-59.7248,0)
  FilletRadius = 0
  Length = 60
  MakeFace = true
  Placement = pos=(-249.595,-274.734,0) rot=(0,0,1;4.80821rad)
  Points = (2) [(-276,0,0),(-216,0,0)]
  Start = (-276,0,0)
  Subdivisions = 0
FEATURE [Part::Part2DObjectPython] Circle045  # Draft 2D object (typed FeaturePython)
  Area = 1.13097
  FirstAngle = 0
  LastAngle = 0
  MakeFace = true
  Placement = pos=(-275.656,-3.58349,0) rot=(0,0,1;4.80821rad)
  Radius = 0.6
FEATURE [Part::Part2DObjectPython] Rectangle046  # Draft 2D object (typed FeaturePython)
  Area = 0
  ChamferSize = 0
  Columns = 1
  FilletRadius = 0
  Height = 6
  Length = 6
  MakeFace = false
  Placement = pos=(-279.129,-17.7588,0) rot=(0,0,1;6.07322rad)
  Rows = 1
FEATURE [Part::Part2DObjectPython] Line046  # Draft 2D object (typed FeaturePython)
  Area = 0
  ChamferSize = 0
  Closed = false
  End = (-216.888,-27.9554,0)
  FilletRadius = 0
  Length = 60
  MakeFace = true
  Placement = pos=(-2.83175,-57.7747,0) rot=(0,0,1;6.07322rad)
  Points = (2) [(-275.57,-15.45,0),(-215.57,-15.45,0)]
  Start = (-275.57,-15.45,0)
  Subdivisions = 0
FEATURE [Part::Part2DObjectPython] Circle046  # Draft 2D object (typed FeaturePython)
  Area = 1.13097
  FirstAngle = 0
  LastAngle = 0
  MakeFace = true
  Placement = pos=(-272.049,-16.2003,0) rot=(0,0,1;6.07322rad)
  Radius = 0.6
FEATURE [Part::Part2DObjectPython] Rectangle047  # Draft 2D object (typed FeaturePython)
  Area = 0
  ChamferSize = 0
  Columns = 1
  FilletRadius = 0
  Height = 6
  Length = 6
  MakeFace = false
  Placement = pos=(-277.649,-33.4157,0) rot=(0,0,1;6.14722rad)
  Rows = 1
FEATURE [Part::Part2DObjectPython] Line047  # Draft 2D object (typed FeaturePython)
  Area = 0
  ChamferSize = 0
  Closed = false
  End = (-214.824,-38.9826,0)
  FilletRadius = 0
  Length = 60
  MakeFace = true
  Placement = pos=(1.65039,-37.46,0) rot=(0,0,1;6.14722rad)
  Points = (2) [(-274.27,-30.85,0),(-214.27,-30.85,0)]
  Start = (-274.27,-30.85,0)
  Subdivisions = 0
FEATURE [Part::Part2DObjectPython] Circle047  # Draft 2D object (typed FeaturePython)
  Area = 1.13097
  FirstAngle = 0
  LastAngle = 0
  MakeFace = true
  Placement = pos=(-270.703,-31.338,0) rot=(0,0,1;6.14722rad)
  Radius = 0.6
FEATURE [Part::Part2DObjectPython] Rectangle048  # Draft 2D object (typed FeaturePython)
  Area = 0
  ChamferSize = 0
  Columns = 1
  FilletRadius = 0
  Height = 6
  Length = 6
  MakeFace = false
  Placement = pos=(-275.342,-48.8986,0) rot=(0,0,1;6.20255rad)
  Rows = 1
FEATURE [Part::Part2DObjectPython] Line048  # Draft 2D object (typed FeaturePython)
  Area = 0
  ChamferSize = 0
  Closed = false
  End = (-212.305,-50.9828,0)
  FilletRadius = 0
  Length = 60
  MakeFace = true
  Placement = pos=(2.8331,-22.0676,0) rot=(0,0,1;6.20255rad)
  Points = (2) [(-272.11,-46.15,0),(-212.11,-46.15,0)]
  Start = (-272.11,-46.15,0)
  Subdivisions = 0
FEATURE [Part::Part2DObjectPython] Circle048  # Draft 2D object (typed FeaturePython)
  Area = 1.13097
  FirstAngle = 0
  LastAngle = 0
  MakeFace = true
  Placement = pos=(-268.522,-46.44,0) rot=(0,0,1;6.20255rad)
  Radius = 0.6
FEATURE [Part::Part2DObjectPython] Rectangle049  # Draft 2D object (typed FeaturePython)
  Area = 0
  ChamferSize = 0
  Columns = 1
  FilletRadius = 0
  Height = 6
  Length = 6
  MakeFace = false
  Placement = pos=(-261.324,-99.4469,0) rot=(0,0,1;0.127409rad)
  Rows = 1
FEATURE [App::FeaturePython] Text014  # WARN: FeaturePython — macro-defined, semantics opaque (R4)
  Placement = pos=(-261.188,-89.1931,0) rot=(0,0,-1;1.07373rad)
  Text = 2
FEATURE [App::FeaturePython] Text015  # WARN: FeaturePython — macro-defined, semantics opaque (R4)
  Placement = pos=(-207.363,-176.926,0) rot=(0,0,-1;6.27708rad)
  Text = 1
FEATURE [Part::Part2DObjectPython] Line049  # Draft 2D object (typed FeaturePython)
  Area = 0
  ChamferSize = 0
  Closed = false
  End = (-199.216,-88.4661,0)
  FilletRadius = 0
  Length = 60
  MakeFace = true
  Placement = pos=(-14.3068,32.0966,0) rot=(0,0,1;0.127409rad)
  Points = (2) [(-258.73,-96.09,0),(-198.73,-96.09,0)]
  Start = (-258.73,-96.09,0)
  Subdivisions = 0
FEATURE [Part::Part2DObjectPython] Circle049  # Draft 2D object (typed FeaturePython)
  Area = 1.13097
  FirstAngle = 0
  LastAngle = 0
  MakeFace = true
  Placement = pos=(-255.159,-95.6326,0) rot=(0,0,1;0.127409rad)
  Radius = 0.6
FEATURE [Part::Part2DObjectPython] Rectangle050  # Draft 2D object (typed FeaturePython)
  Area = 0
  ChamferSize = 0
  Columns = 1
  FilletRadius = 0
  Height = 6
  Length = 6
  MakeFace = false
  Placement = pos=(-255.327,-113.934,0) rot=(0,0,1;0.190764rad)
  Rows = 1
FEATURE [Part::Part2DObjectPython] Line050  # Draft 2D object (typed FeaturePython)
  Area = 0
  ChamferSize = 0
  Closed = false
  End = (-194.038,-99.0434,0)
  FilletRadius = 0
  Length = 60
  MakeFace = true
  Placement = pos=(-25.5253,45.9587,0) rot=(0,0,1;0.190764rad)
  Points = (2) [(-252.95,-110.42,0),(-192.95,-110.42,0)]
  Start = (-252.95,-110.42,0)
  Subdivisions = 0
FEATURE [Part::Part2DObjectPython] Circle050  # Draft 2D object (typed FeaturePython)
  Area = 1.13097
  FirstAngle = 0
  LastAngle = 0
  MakeFace = true
  Placement = pos=(-249.415,-109.737,0) rot=(0,0,1;0.190764rad)
  Radius = 0.6
FEATURE [Part::Part2DObjectPython] Rectangle051  # Draft 2D object (typed FeaturePython)
  Area = 0
  ChamferSize = 0
  Columns = 1
  FilletRadius = 0
  Height = 6
  Length = 6
  MakeFace = false
  Placement = pos=(-248.517,-128.069,0) rot=(0,0,1;0.254818rad)
  Rows = 1
FEATURE [Part::Part2DObjectPython] Line051  # Draft 2D object (typed FeaturePython)
  Area = 0
  ChamferSize = 0
  Closed = false
  End = (-188.307,-109.286,0)
  FilletRadius = 0
  Length = 60
  MakeFace = true
  Placement = pos=(-39.3154,58.085,0) rot=(0,0,1;0.254818rad)
  Points = (2) [(-246.37,-124.41,0),(-186.37,-124.41,0)]
  Start = (-246.37,-124.41,0)
  Subdivisions = 0
FEATURE [Part::Part2DObjectPython] Circle051  # Draft 2D object (typed FeaturePython)
  Area = 1.13097
  FirstAngle = 0
  LastAngle = 0
  MakeFace = true
  Placement = pos=(-242.886,-123.503,0) rot=(0,0,1;0.254818rad)
  Radius = 0.6
FEATURE [Part::Part2DObjectPython] Rectangle052  # Draft 2D object (typed FeaturePython)
  Area = 0
  ChamferSize = 0
  Columns = 1
  FilletRadius = 0
  Height = 6
  Length = 6
  MakeFace = false
  Placement = pos=(-240.932,-141.788,0) rot=(0,0,1;0.317999rad)
  Rows = 1
FEATURE [Part::Part2DObjectPython] Line052  # Draft 2D object (typed FeaturePython)
  Area = 0
  ChamferSize = 0
  Closed = false
  End = (-182.028,-119.24,0)
  FilletRadius = 0
  Length = 60
  MakeFace = true
  Placement = pos=(-55.1317,67.8146,0) rot=(0,0,1;0.317999rad)
  Points = (2) [(-239.02,-138,0),(-179.02,-138,0)]
  Start = (-239.02,-138,0)
  Subdivisions = 0
FEATURE [Part::Part2DObjectPython] Circle052  # Draft 2D object (typed FeaturePython)
  Area = 1.13097
  FirstAngle = 0
  LastAngle = 0
  MakeFace = true
  Placement = pos=(-235.6,-136.874,0) rot=(0,0,1;0.317999rad)
  Radius = 0.6
FEATURE [Part::Part2DObjectPython] Rectangle053  # Draft 2D object (typed FeaturePython)
  Area = 0
  ChamferSize = 0
  Columns = 1
  FilletRadius = 0
  Height = 6
  Length = 6
  MakeFace = false
  Placement = pos=(-232.589,-155.06,0) rot=(0,0,1;0.381005rad)
  Rows = 1
FEATURE [Part::Part2DObjectPython] Line053  # Draft 2D object (typed FeaturePython)
  Area = 0
  ChamferSize = 0
  Closed = false
  End = (-175.223,-128.849,0)
  FilletRadius = 0
  Length = 60
  MakeFace = true
  Placement = pos=(-72.7684,75.029,0) rot=(0,0,1;0.381005rad)
  Points = (2) [(-230.92,-151.16,0),(-170.92,-151.16,0)]
  Start = (-230.92,-151.16,0)
  Subdivisions = 0
FEATURE [Part::Part2DObjectPython] Circle053  # Draft 2D object (typed FeaturePython)
  Area = 1.13097
  FirstAngle = 0
  LastAngle = 0
  MakeFace = true
  Placement = pos=(-227.578,-149.821,0) rot=(0,0,1;0.381005rad)
  Radius = 0.6
FEATURE [Part::Part2DObjectPython] Rectangle054  # Draft 2D object (typed FeaturePython)
  Area = 0
  ChamferSize = 0
  Columns = 1
  FilletRadius = 0
  Height = 6
  Length = 6
  MakeFace = false
  Placement = pos=(-223.523,-167.847,0) rot=(0,0,1;0.443488rad)
  Rows = 1
FEATURE [Part::Part2DObjectPython] Line054  # Draft 2D object (typed FeaturePython)
  Area = 0
  ChamferSize = 0
  Closed = false
  End = (-167.904,-138.104,0)
  FilletRadius = 0
  Length = 60
  MakeFace = true
  Placement = pos=(-91.7927,79.4507,0) rot=(0,0,1;0.443488rad)
  Points = (2) [(-222.1,-163.85,0),(-162.1,-163.85,0)]
  Start = (-222.1,-163.85,0)
  Subdivisions = 0
FEATURE [Part::Part2DObjectPython] Circle054  # Draft 2D object (typed FeaturePython)
  Area = 1.13097
  FirstAngle = 0
  LastAngle = 0
  MakeFace = true
  Placement = pos=(-218.848,-162.305,0) rot=(0,0,1;0.443488rad)
  Radius = 0.6
FEATURE [Part::Part2DObjectPython] Rectangle055  # Draft 2D object (typed FeaturePython)
  Area = 0
  ChamferSize = 0
  Columns = 1
  FilletRadius = 0
  Height = 6
  Length = 6
  MakeFace = false
  Placement = pos=(-213.757,-180.096,0) rot=(0,0,1;0.5044rad)
  Rows = 1
FEATURE [Part::Part2DObjectPython] Line055  # Draft 2D object (typed FeaturePython)
  Area = 0
  ChamferSize = 0
  Closed = false
  End = (-160.052,-147.023,0)
  FilletRadius = 0
  Length = 60
  MakeFace = true
  Placement = pos=(-111.541,80.8154,0) rot=(0,0,1;0.5044rad)
  Points = (2) [(-212.58,-176.02,0),(-152.58,-176.02,0)]
  Start = (-212.58,-176.02,0)
  Subdivisions = 0
FEATURE [Part::Part2DObjectPython] Circle055  # Draft 2D object (typed FeaturePython)
  Area = 1.13097
  FirstAngle = 0
  LastAngle = 0
  MakeFace = true
  Placement = pos=(-209.428,-174.28,0) rot=(0,0,1;0.5044rad)
  Radius = 0.6
FEATURE [Part::Part2DObjectPython] Rectangle056  # Draft 2D object (typed FeaturePython)
  Area = 0
  ChamferSize = 0
  Columns = 1
  FilletRadius = 0
  Height = 6
  Length = 6
  MakeFace = false
  Placement = pos=(-176.938,-216.722,0) rot=(0,0,1;0.567407rad)
  Rows = 1
FEATURE [App::FeaturePython] Text016  # WARN: FeaturePython — macro-defined, semantics opaque (R4)
  Placement = pos=(-181.597,-207.836,0) rot=(0,0,-1;0.550128rad)
  Text = 2
FEATURE [App::FeaturePython] Text017  # WARN: FeaturePython — macro-defined, semantics opaque (R4)
  Placement = pos=(-91.1209,-256.902,0) rot=(0,0,-1;5.75348rad)
  Text = 2
FEATURE [Part::Part2DObjectPython] Line056  # Draft 2D object (typed FeaturePython)
  Area = 0
  ChamferSize = 0
  Closed = false
  End = (-125.422,-180.333,0)
  FilletRadius = 0
  Length = 60
  MakeFace = true
  Placement = pos=(-141.833,61.2896,0) rot=(0,0,1;0.567407rad)
  Points = (2) [(-176.02,-212.58,0),(-116.02,-212.58,0)]
  Start = (-176.02,-212.58,0)
  Subdivisions = 0
FEATURE [Part::Part2DObjectPython] Circle056  # Draft 2D object (typed FeaturePython)
  Area = 1.13097
  FirstAngle = 0
  LastAngle = 0
  MakeFace = true
  Placement = pos=(-172.984,-210.645,0) rot=(0,0,1;0.567407rad)
  Radius = 0.6
FEATURE [Part::Part2DObjectPython] Rectangle057  # Draft 2D object (typed FeaturePython)
  Area = 0
  ChamferSize = 0
  Columns = 1
  FilletRadius = 0
  Height = 6
  Length = 6
  MakeFace = false
  Placement = pos=(-165.977,-225.771,0) rot=(0,0,1;0.260229rad)
  Rows = 1
FEATURE [Part::Part2DObjectPython] Line057  # Draft 2D object (typed FeaturePython)
  Area = 0
  ChamferSize = 0
  Closed = false
  End = (-105.87,-206.662,0)
  FilletRadius = 0
  Length = 60
  MakeFace = true
  Placement = pos=(-62.6633,34.681,0) rot=(0,0,1;0.260229rad)
  Points = (2) [(-163.85,-222.1,0),(-103.85,-222.1,0)]
  Start = (-163.85,-222.1,0)
  Subdivisions = 0
FEATURE [Part::Part2DObjectPython] Circle057  # Draft 2D object (typed FeaturePython)
  Area = 1.13097
  FirstAngle = 0
  LastAngle = 0
  MakeFace = true
  Placement = pos=(-160.371,-221.174,0) rot=(0,0,1;0.260229rad)
  Radius = 0.6
FEATURE [Part::Part2DObjectPython] Rectangle058  # Draft 2D object (typed FeaturePython)
  Area = 0
  ChamferSize = 0
  Columns = 1
  FilletRadius = 0
  Height = 6
  Length = 6
  MakeFace = false
  Placement = pos=(-155.393,-231.201,0) rot=(0,0,1;5.56411rad)
  Rows = 1
FEATURE [Part::Part2DObjectPython] Line058  # Draft 2D object (typed FeaturePython)
  Area = 0
  ChamferSize = 0
  Closed = false
  End = (-106.015,-270.441,0)
  FilletRadius = 0
  Length = 60
  MakeFace = true
  Placement = pos=(114.68,-156.74,0) rot=(0,0,1;5.56411rad)
  Points = (2) [(-151.16,-230.92,0),(-91.16,-230.92,0)]
  Start = (-151.16,-230.92,0)
  Subdivisions = 0
FEATURE [Part::Part2DObjectPython] Circle058  # Draft 2D object (typed FeaturePython)
  Area = 1.13097
  FirstAngle = 0
  LastAngle = 0
  MakeFace = true
  Placement = pos=(-148.451,-233.291,0) rot=(0,0,1;5.56411rad)
  Radius = 0.6
FEATURE [Part::Part2DObjectPython] Rectangle059  # Draft 2D object (typed FeaturePython)
  Area = 0
  ChamferSize = 0
  Columns = 1
  FilletRadius = 0
  Height = 6
  Length = 6
  MakeFace = false
  Placement = pos=(-141.889,-237.323,0) rot=(0,0,1;5.08641rad)
  Rows = 1
FEATURE [Part::Part2DObjectPython] Line059  # Draft 2D object (typed FeaturePython)
  Area = 0
  ChamferSize = 0
  Closed = false
  End = (-116.078,-294.872,0)
  FilletRadius = 0
  Length = 60
  MakeFace = true
  Placement = pos=(134.916,-280.15,0) rot=(0,0,1;5.08641rad)
  Points = (2) [(-138,-239.02,0),(-78,-239.02,0)]
  Start = (-138,-239.02,0)
  Subdivisions = 0
FEATURE [Part::Part2DObjectPython] Circle059  # Draft 2D object (typed FeaturePython)
  Area = 1.13097
  FirstAngle = 0
  LastAngle = 0
  MakeFace = true
  Placement = pos=(-136.685,-242.371,0) rot=(0,0,1;5.08641rad)
  Radius = 0.6
FEATURE [Part::Part2DObjectPython] Rectangle060  # Draft 2D object (typed FeaturePython)
  Area = 0
  ChamferSize = 0
  Columns = 1
  FilletRadius = 0
  Height = 6
  Length = 6
  MakeFace = false
  Placement = pos=(-128.219,-244.502,0) rot=(0,0,1;5.04173rad)
  Rows = 1
FEATURE [Part::Part2DObjectPython] Line060  # Draft 2D object (typed FeaturePython)
  Area = 0
  ChamferSize = 0
  Closed = false
  End = (-105.005,-303.145,0)
  FilletRadius = 0
  Length = 60
  MakeFace = true
  Placement = pos=(148.956,-284.412,0) rot=(0,0,1;5.04173rad)
  Points = (2) [(-124.41,-246.37,0),(-64.41,-246.37,0)]
  Start = (-124.41,-246.37,0)
  Subdivisions = 0
FEATURE [Part::Part2DObjectPython] Circle060  # Draft 2D object (typed FeaturePython)
  Area = 1.13097
  FirstAngle = 0
  LastAngle = 0
  MakeFace = true
  Placement = pos=(-123.246,-249.777,0) rot=(0,0,1;5.04173rad)
  Radius = 0.6
FEATURE [Part::Part2DObjectPython] Rectangle061  # Draft 2D object (typed FeaturePython)
  Area = 0
  ChamferSize = 0
  Columns = 1
  FilletRadius = 0
  Height = 6
  Length = 6
  MakeFace = false
  Placement = pos=(-114.365,-251.39,0) rot=(0,0,1;5.12115rad)
  Rows = 1
FEATURE [Part::Part2DObjectPython] Line061  # Draft 2D object (typed FeaturePython)
  Area = 0
  ChamferSize = 0
  Closed = false
  End = (-86.5719,-308.007,0)
  FilletRadius = 0
  Length = 60
  MakeFace = true
  Placement = pos=(165.579,-253.734,0) rot=(0,0,1;5.12115rad)
  Points = (2) [(-110.42,-252.95,0),(-50.42,-252.95,0)]
  Start = (-110.42,-252.95,0)
  Subdivisions = 0
FEATURE [Part::Part2DObjectPython] Circle061  # Draft 2D object (typed FeaturePython)
  Area = 1.13097
  FirstAngle = 0
  LastAngle = 0
  MakeFace = true
  Placement = pos=(-108.989,-256.253,0) rot=(0,0,1;5.12115rad)
  Radius = 0.6
FEATURE [Part::Part2DObjectPython] Rectangle062  # Draft 2D object (typed FeaturePython)
  Area = 0
  ChamferSize = 0
  Columns = 1
  FilletRadius = 0
  Height = 6
  Length = 6
  MakeFace = false
  Placement = pos=(-100.205,-257.696,0) rot=(0,0,1;5.2517rad)
  Rows = 1
FEATURE [Part::Part2DObjectPython] Line062  # Draft 2D object (typed FeaturePython)
  Area = 0
  ChamferSize = 0
  Closed = false
  End = (-65.2775,-310.214,0)
  FilletRadius = 0
  Length = 60
  MakeFace = true
  Placement = pos=(175.263,-208.313,0) rot=(0,0,1;5.2517rad)
  Points = (2) [(-96.09,-258.73,0),(-36.09,-258.73,0)]
  Start = (-96.09,-258.73,0)
  Subdivisions = 0
FEATURE [Part::Part2DObjectPython] Circle062  # Draft 2D object (typed FeaturePython)
  Area = 1.13097
  FirstAngle = 0
  LastAngle = 0
  MakeFace = true
  Placement = pos=(-94.2413,-261.819,0) rot=(0,0,1;5.2517rad)
  Radius = 0.6
FEATURE [Part::Part2DObjectPython] Rectangle063  # Draft 2D object (typed FeaturePython)
  Area = 0
  ChamferSize = 0
  Columns = 1
  FilletRadius = 0
  Height = 6
  Length = 6
  MakeFace = false
  Placement = pos=(-50.1281,-273.585,0) rot=(0,0,1;5.85279rad)
  Rows = 1
FEATURE [App::FeaturePython] Text018  # WARN: FeaturePython — macro-defined, semantics opaque (R4)
  Placement = pos=(-53.3517,-270.79,0) rot=(0,0,1;6.25666rad)
  Text = 2
FEATURE [App::FeaturePython] Text019  # WARN: FeaturePython — macro-defined, semantics opaque (R4)
  Placement = pos=(49.5386,-268.047,0) rot=(0,0,1;1.05331rad)
  Text = 3
FEATURE [Part::Part2DObjectPython] Line063  # Draft 2D object (typed FeaturePython)
  Area = 0
  ChamferSize = 0
  Closed = false
  End = (8.37798,-297.144,0)
  FilletRadius = 0
  Length = 60
  MakeFace = true
  Placement = pos=(109.324,-44.0718,0) rot=(0,0,1;5.85279rad)
  Points = (2) [(-46.15,-272.11,0),(13.85,-272.11,0)]
  Start = (-46.15,-272.11,0)
  Subdivisions = 0
FEATURE [Part::Part2DObjectPython] Circle063  # Draft 2D object (typed FeaturePython)
  Area = 1.13097
  FirstAngle = 0
  LastAngle = 0
  MakeFace = true
  Placement = pos=(-42.8783,-273.612,0) rot=(0,0,1;5.85279rad)
  Radius = 0.6
FEATURE [Part::Part2DObjectPython] Rectangle064  # Draft 2D object (typed FeaturePython)
  Area = 0
  ChamferSize = 0
  Columns = 1
  FilletRadius = 0
  Height = 6
  Length = 6
  MakeFace = false
  Placement = pos=(-34.4538,-276.509,0) rot=(0,0,1;6.05368rad)
  Rows = 1
FEATURE [Part::Part2DObjectPython] Line064  # Draft 2D object (typed FeaturePython)
  Area = 0
  ChamferSize = 0
  Closed = false
  End = (27.5767,-287.92,0)
  FilletRadius = 0
  Length = 60
  MakeFace = true
  Placement = pos=(61.5878,-14.2104,0) rot=(0,0,1;6.05368rad)
  Points = (2) [(-30.85,-274.27,0),(29.15,-274.27,0)]
  Start = (-30.85,-274.27,0)
  Subdivisions = 0
FEATURE [Part::Part2DObjectPython] Circle064  # Draft 2D object (typed FeaturePython)
  Area = 1.13097
  FirstAngle = 0
  LastAngle = 0
  MakeFace = true
  Placement = pos=(-27.3444,-275.089,0) rot=(0,0,1;6.05368rad)
  Radius = 0.6
FEATURE [Part::Part2DObjectPython] Rectangle065  # Draft 2D object (typed FeaturePython)
  Area = 0
  ChamferSize = 0
  Columns = 1
  FilletRadius = 0
  Height = 6
  Length = 6
  MakeFace = false
  Placement = pos=(-18.5483,-278.468,0) rot=(0,0,1;6.24985rad)
  Rows = 1
FEATURE [Part::Part2DObjectPython] Line065  # Draft 2D object (typed FeaturePython)
  Area = 0
  ChamferSize = 0
  Closed = false
  End = (44.5167,-277.57,0)
  FilletRadius = 0
  Length = 60
  MakeFace = true
  Placement = pos=(9.17606,-0.668045,0) rot=(0,0,1;6.24985rad)
  Points = (2) [(-15.45,-275.57,0),(44.55,-275.57,0)]
  Start = (-15.45,-275.57,0)
  Subdivisions = 0
FEATURE [Part::Part2DObjectPython] Circle065  # Draft 2D object (typed FeaturePython)
  Area = 1.13097
  FirstAngle = 0
  LastAngle = 0
  MakeFace = true
  Placement = pos=(-11.852,-275.69,0) rot=(0,0,1;6.24985rad)
  Radius = 0.6
FEATURE [Part::Part2DObjectPython] Rectangle066  # Draft 2D object (typed FeaturePython)
  Area = 0
  ChamferSize = 0
  Columns = 1
  FilletRadius = 0
  Height = 6
  Length = 6
  MakeFace = false
  Placement = pos=(-2.58158,-279.367,0) rot=(0,0,1;0.131249rad)
  Rows = 1
FEATURE [Part::Part2DObjectPython] Line066  # Draft 2D object (typed FeaturePython)
  Area = 0
  ChamferSize = 0
  Closed = false
  End = (59.484,-268.148,0)
  FilletRadius = 0
  Length = 60
  MakeFace = true
  Placement = pos=(-36.1207,-2.37381,0) rot=(0,0,1;0.131249rad)
  Points = (2) [(0,-276,0),(60,-276,0)]
  Start = (0,-276,0)
  Subdivisions = 0
FEATURE [Part::Part2DObjectPython] Circle066  # Draft 2D object (typed FeaturePython)
  Area = 1.13097
  FirstAngle = 0
  LastAngle = 0
  MakeFace = true
  Placement = pos=(3.56904,-275.529,0) rot=(0,0,1;0.131249rad)
  Radius = 0.6
FEATURE [Part::Part2DObjectPython] Rectangle067  # Draft 2D object (typed FeaturePython)
  Area = 0
  ChamferSize = 0
  Columns = 1
  FilletRadius = 0
  Height = 6
  Length = 6
  MakeFace = false
  Placement = pos=(12.7394,-278.834,0) rot=(0,0,1;0.092328rad)
  Rows = 1
FEATURE [Part::Part2DObjectPython] Line067  # Draft 2D object (typed FeaturePython)
  Area = 0
  ChamferSize = 0
  Closed = false
  End = (75.1944,-270.038,0)
  FilletRadius = 0
  Length = 60
  MakeFace = true
  Placement = pos=(-25.3409,-2.59815,0) rot=(0,0,1;0.092328rad)
  Points = (2) [(15.45,-275.57,0),(75.45,-275.57,0)]
  Start = (15.45,-275.57,0)
  Subdivisions = 0
FEATURE [Part::Part2DObjectPython] Circle067  # Draft 2D object (typed FeaturePython)
  Area = 1.13097
  FirstAngle = 0
  LastAngle = 0
  MakeFace = true
  Placement = pos=(19.0347,-275.238,0) rot=(0,0,1;0.092328rad)
  Radius = 0.6
FEATURE [Part::Part2DObjectPython] Rectangle068  # Draft 2D object (typed FeaturePython)
  Area = 0
  ChamferSize = 0
  Columns = 1
  FilletRadius = 0
  Height = 6
  Length = 6
  MakeFace = false
  Placement = pos=(33.8505,-271.271,0) rot=(0,0,1;3.14142rad)
  Rows = 1
FEATURE [Part::Part2DObjectPython] Line068  # Draft 2D object (typed FeaturePython)
  Area = 0
  ChamferSize = 0
  Closed = false
  End = (-29.15,-274.26,0)
  FilletRadius = 0
  Length = 60
  MakeFace = true
  Placement = pos=(61.6521,-548.545,0) rot=(0,0,1;3.14142rad)
  Points = (2) [(30.85,-274.27,0),(90.85,-274.27,0)]
  Start = (30.85,-274.27,0)
  Subdivisions = 0
FEATURE [Part::Part2DObjectPython] Circle068  # Draft 2D object (typed FeaturePython)
  Area = 1.13097
  FirstAngle = 0
  LastAngle = 0
  MakeFace = true
  Placement = pos=(27.25,-274.269,0) rot=(0,0,1;3.14142rad)
  Radius = 0.6
FEATURE [Part::Part2DObjectPython] Rectangle069  # Draft 2D object (typed FeaturePython)
  Area = 0
  ChamferSize = 0
  Columns = 1
  FilletRadius = 0
  Height = 6
  Length = 6
  MakeFace = false
  Placement = pos=(49.1505,-269.111,0) rot=(0,0,1;3.14142rad)
  Rows = 1
FEATURE [Part::Part2DObjectPython] Line069  # Draft 2D object (typed FeaturePython)
  Area = 0
  ChamferSize = 0
  Closed = false
  End = (-13.85,-272.1,0)
  FilletRadius = 0
  Length = 60
  MakeFace = true
  Placement = pos=(92.2525,-544.228,0) rot=(0,0,1;3.14142rad)
  Points = (2) [(46.15,-272.11,0),(106.15,-272.11,0)]
  Start = (46.15,-272.11,0)
  Subdivisions = 0
FEATURE [Part::Part2DObjectPython] Circle069  # Draft 2D object (typed FeaturePython)
  Area = 1.13097
  FirstAngle = 0
  LastAngle = 0
  MakeFace = true
  Placement = pos=(42.55,-272.109,0) rot=(0,0,1;3.14142rad)
  Radius = 0.6
FEATURE [Part::Part2DObjectPython] Rectangle070  # Draft 2D object (typed FeaturePython)
  Area = 0
  ChamferSize = 0
  Columns = 1
  FilletRadius = 0
  Height = 6
  Length = 6
  MakeFace = false
  Placement = pos=(99.0926,-255.733,0) rot=(0,0,1;3.14072rad)
  Rows = 1
FEATURE [App::FeaturePython] Text020  # WARN: FeaturePython — macro-defined, semantics opaque (R4)
  Placement = pos=(89.1931,-261.188,0) rot=(0,0,-1;5.78612rad)
  Text = 2
FEATURE [App::FeaturePython] Text021  # WARN: FeaturePython — macro-defined, semantics opaque (R4)
  Placement = pos=(176.926,-207.363,0) rot=(0,0,1;1.57691rad)
  Text = 4
FEATURE [Part::Part2DObjectPython] Line070  # Draft 2D object (typed FeaturePython)
  Area = 0
  ChamferSize = 0
  Closed = false
  End = (36.09,-258.678,0)
  FilletRadius = 0
  Length = 60
  MakeFace = true
  Placement = pos=(191.954,-517.544,0) rot=(0,0,1;3.14072rad)
  Points = (2) [(96.09,-258.73,0),(156.09,-258.73,0)]
  Start = (96.09,-258.73,0)
  Subdivisions = 0
FEATURE [Part::Part2DObjectPython] Circle070  # Draft 2D object (typed FeaturePython)
  Area = 1.13097
  FirstAngle = 0
  LastAngle = 0
  MakeFace = true
  Placement = pos=(92.49,-258.727,0) rot=(0,0,1;3.14072rad)
  Radius = 0.6
FEATURE [Part::Part2DObjectPython] Rectangle071  # Draft 2D object (typed FeaturePython)
  Area = 0
  ChamferSize = 0
  Columns = 1
  FilletRadius = 0
  Height = 6
  Length = 6
  MakeFace = false
  Placement = pos=(106.635,-251.033,0) rot=(0,0,1;5.02899rad)
  Rows = 1
FEATURE [Part::Part2DObjectPython] Line071  # Draft 2D object (typed FeaturePython)
  Area = 0
  ChamferSize = 0
  Closed = false
  End = (129.1,-309.968,0)
  FilletRadius = 0
  Length = 60
  MakeFace = true
  Placement = pos=(316.42,-69.2646,0) rot=(0,0,1;5.02899rad)
  Points = (2) [(110.42,-252.95,0),(170.42,-252.95,0)]
  Start = (110.42,-252.95,0)
  Subdivisions = 0
FEATURE [Part::Part2DObjectPython] Circle071  # Draft 2D object (typed FeaturePython)
  Area = 1.13097
  FirstAngle = 0
  LastAngle = 0
  MakeFace = true
  Placement = pos=(111.541,-256.371,0) rot=(0,0,1;5.02899rad)
  Radius = 0.6
FEATURE [Part::Part2DObjectPython] Rectangle072  # Draft 2D object (typed FeaturePython)
  Area = 0
  ChamferSize = 0
  Columns = 1
  FilletRadius = 0
  Height = 6
  Length = 6
  MakeFace = false
  Placement = pos=(128.638,-246.019,0) rot=(0,0,1;2.43892rad)
  Rows = 1
FEATURE [Part::Part2DObjectPython] Line072  # Draft 2D object (typed FeaturePython)
  Area = 0
  ChamferSize = 0
  Closed = false
  End = (78.6228,-207.595,0)
  FilletRadius = 0
  Length = 60
  MakeFace = true
  Placement = pos=(60.1313,-514.781,0) rot=(0,0,1;2.43892rad)
  Points = (2) [(124.41,-246.37,0),(184.41,-246.37,0)]
  Start = (124.41,-246.37,0)
  Subdivisions = 0
FEATURE [Part::Part2DObjectPython] Circle072  # Draft 2D object (typed FeaturePython)
  Area = 1.13097
  FirstAngle = 0
  LastAngle = 0
  MakeFace = true
  Placement = pos=(121.663,-244.043,0) rot=(0,0,1;2.43892rad)
  Radius = 0.6
FEATURE [Part::Part2DObjectPython] Rectangle073  # Draft 2D object (typed FeaturePython)
  Area = 0
  ChamferSize = 0
  Columns = 1
  FilletRadius = 0
  Height = 6
  Length = 6
  MakeFace = false
  Placement = pos=(142.149,-239.907,0) rot=(0,0,1;2.14553rad)
  Rows = 1
FEATURE [Part::Part2DObjectPython] Line073  # Draft 2D object (typed FeaturePython)
  Area = 0
  ChamferSize = 0
  Closed = false
  End = (105.383,-188.66,0)
  FilletRadius = 0
  Length = 60
  MakeFace = true
  Placement = pos=(12.4008,-484.783,0) rot=(0,0,1;2.14553rad)
  Points = (2) [(138,-239.02,0),(198,-239.02,0)]
  Start = (138,-239.02,0)
  Subdivisions = 0
FEATURE [Part::Part2DObjectPython] Circle073  # Draft 2D object (typed FeaturePython)
  Area = 1.13097
  FirstAngle = 0
  LastAngle = 0
  MakeFace = true
  Placement = pos=(136.043,-235.998,0) rot=(0,0,1;2.14553rad)
  Radius = 0.6
FEATURE [Part::Part2DObjectPython] Rectangle074  # Draft 2D object (typed FeaturePython)
  Area = 0
  ChamferSize = 0
  Columns = 1
  FilletRadius = 0
  Height = 6
  Length = 6
  MakeFace = false
  Placement = pos=(155.401,-231.025,0) rot=(0,0,1;2.33141rad)
  Rows = 1
FEATURE [Part::Part2DObjectPython] Line074  # Draft 2D object (typed FeaturePython)
  Area = 0
  ChamferSize = 0
  Closed = false
  End = (109.798,-187.455,0)
  FilletRadius = 0
  Length = 60
  MakeFace = true
  Placement = pos=(88.0833,-499.611,0) rot=(0,0,1;2.33141rad)
  Points = (2) [(151.16,-230.92,0),(211.16,-230.92,0)]
  Start = (151.16,-230.92,0)
  Subdivisions = 0
FEATURE [Part::Part2DObjectPython] Circle074  # Draft 2D object (typed FeaturePython)
  Area = 1.13097
  FirstAngle = 0
  LastAngle = 0
  MakeFace = true
  Placement = pos=(148.678,-228.312,0) rot=(0,0,1;2.33141rad)
  Radius = 0.6
FEATURE [Part::Part2DObjectPython] Rectangle075  # Draft 2D object (typed FeaturePython)
  Area = 0
  ChamferSize = 0
  Columns = 1
  FilletRadius = 0
  Height = 6
  Length = 6
  MakeFace = false
  Placement = pos=(168.051,-221.504,0) rot=(0,0,1;2.49704rad)
  Rows = 1
FEATURE [Part::Part2DObjectPython] Line075  # Draft 2D object (typed FeaturePython)
  Area = 0
  ChamferSize = 0
  Closed = false
  End = (115.888,-186.05,0)
  FilletRadius = 0
  Length = 60
  MakeFace = true
  Placement = pos=(161.38,-498.088,0) rot=(0,0,1;2.49704rad)
  Points = (2) [(163.85,-222.1,0),(223.85,-222.1,0)]
  Start = (163.85,-222.1,0)
  Subdivisions = 0
FEATURE [Part::Part2DObjectPython] Circle075  # Draft 2D object (typed FeaturePython)
  Area = 1.13097
  FirstAngle = 0
  LastAngle = 0
  MakeFace = true
  Placement = pos=(160.972,-219.937,0) rot=(0,0,1;2.49704rad)
  Radius = 0.6
FEATURE [Part::Part2DObjectPython] Rectangle076  # Draft 2D object (typed FeaturePython)
  Area = 0
  ChamferSize = 0
  Columns = 1
  FilletRadius = 0
  Height = 6
  Length = 6
  MakeFace = false
  Placement = pos=(180.075,-211.331,0) rot=(0,0,1;2.65499rad)
  Rows = 1
FEATURE [Part::Part2DObjectPython] Line076  # Draft 2D object (typed FeaturePython)
  Area = 0
  ChamferSize = 0
  Closed = false
  End = (122.984,-184.523,0)
  FilletRadius = 0
  Length = 60
  MakeFace = true
  Placement = pos=(232.202,-482.796,0) rot=(0,0,1;2.65499rad)
  Points = (2) [(176.02,-212.58,0),(236.02,-212.58,0)]
  Start = (176.02,-212.58,0)
  Subdivisions = 0
FEATURE [Part::Part2DObjectPython] Circle076  # Draft 2D object (typed FeaturePython)
  Area = 1.13097
  FirstAngle = 0
  LastAngle = 0
  MakeFace = true
  Placement = pos=(172.838,-210.897,0) rot=(0,0,1;2.65499rad)
  Radius = 0.6
FEATURE [Part::Part2DObjectPython] Rectangle077  # Draft 2D object (typed FeaturePython)
  Area = 0
  ChamferSize = 0
  Columns = 1
  FilletRadius = 0
  Height = 6
  Length = 6
  MakeFace = false
  Placement = pos=(215.621,-173.061,0) rot=(0,0,1;3.12798rad)
  Rows = 1
FEATURE [App::FeaturePython] Text022  # WARN: FeaturePython — macro-defined, semantics opaque (R4)
  Placement = pos=(207.836,-181.597,0) rot=(0,0,-1;5.26252rad)
  Text = 2
FEATURE [App::FeaturePython] Text023  # WARN: FeaturePython — macro-defined, semantics opaque (R4)
  Placement = pos=(256.902,-91.1209,0) rot=(0,0,1;2.1005rad)
  Text = 5
FEATURE [Part::Part2DObjectPython] Line077  # Draft 2D object (typed FeaturePython)
  Area = 0
  ChamferSize = 0
  Closed = false
  End = (152.586,-175.203,0)
  FilletRadius = 0
  Length = 60
  MakeFace = true
  Placement = pos=(422.744,-354.918,0) rot=(0,0,1;3.12798rad)
  Points = (2) [(212.58,-176.02,0),(272.58,-176.02,0)]
  Start = (212.58,-176.02,0)
  Subdivisions = 0
FEATURE [Part::Part2DObjectPython] Circle077  # Draft 2D object (typed FeaturePython)
  Area = 1.13097
  FirstAngle = 0
  LastAngle = 0
  MakeFace = true
  Placement = pos=(208.98,-175.971,0) rot=(0,0,1;3.12798rad)
  Radius = 0.6
FEATURE [Part::Part2DObjectPython] Rectangle078  # Draft 2D object (typed FeaturePython)
  Area = 0
  ChamferSize = 0
  Columns = 1
  FilletRadius = 0
  Height = 6
  Length = 6
  MakeFace = false
  Placement = pos=(224.612,-160.431,0) rot=(0,0,1;3.29326rad)
  Rows = 1
FEATURE [Part::Part2DObjectPython] Line078  # Draft 2D object (typed FeaturePython)
  Area = 0
  ChamferSize = 0
  Closed = false
  End = (162.789,-172.915,0)
  FilletRadius = 0
  Length = 60
  MakeFace = true
  Placement = pos=(466.406,-292.262,0) rot=(0,0,1;3.29326rad)
  Points = (2) [(222.1,-163.85,0),(282.1,-163.85,0)]
  Start = (222.1,-163.85,0)
  Subdivisions = 0
FEATURE [Part::Part2DObjectPython] Circle078  # Draft 2D object (typed FeaturePython)
  Area = 1.13097
  FirstAngle = 0
  LastAngle = 0
  MakeFace = true
  Placement = pos=(218.541,-164.394,0) rot=(0,0,1;3.29326rad)
  Radius = 0.6
FEATURE [Part::Part2DObjectPython] Rectangle079  # Draft 2D object (typed FeaturePython)
  Area = 0
  ChamferSize = 0
  Columns = 1
  FilletRadius = 0
  Height = 6
  Length = 6
  MakeFace = false
  Placement = pos=(232.944,-147.431,0) rot=(0,0,1;3.42957rad)
  Rows = 1
FEATURE [Part::Part2DObjectPython] Line079  # Draft 2D object (typed FeaturePython)
  Area = 0
  ChamferSize = 0
  Closed = false
  End = (173.391,-168.201,0)
  FilletRadius = 0
  Length = 60
  MakeFace = true
  Placement = pos=(495.262,-230.51,0) rot=(0,0,1;3.42957rad)
  Points = (2) [(230.92,-151.16,0),(290.92,-151.16,0)]
  Start = (230.92,-151.16,0)
  Subdivisions = 0
FEATURE [Part::Part2DObjectPython] Circle079  # Draft 2D object (typed FeaturePython)
  Area = 1.13097
  FirstAngle = 0
  LastAngle = 0
  MakeFace = true
  Placement = pos=(227.468,-152.182,0) rot=(0,0,1;3.42957rad)
  Radius = 0.6
FEATURE [Part::Part2DObjectPython] Rectangle080  # Draft 2D object (typed FeaturePython)
  Area = 0
  ChamferSize = 0
  Columns = 1
  FilletRadius = 0
  Height = 6
  Length = 6
  MakeFace = false
  Placement = pos=(240.533,-134.036,0) rot=(0,0,1;3.56239rad)
  Rows = 1
FEATURE [Part::Part2DObjectPython] Line080  # Draft 2D object (typed FeaturePython)
  Area = 0
  ChamferSize = 0
  Closed = false
  End = (184.254,-162.509,0)
  FilletRadius = 0
  Length = 60
  MakeFace = true
  Placement = pos=(513.56,-166.324,0) rot=(0,0,1;3.56239rad)
  Points = (2) [(239.02,-138,0),(299.02,-138,0)]
  Start = (239.02,-138,0)
  Subdivisions = 0
FEATURE [Part::Part2DObjectPython] Circle080  # Draft 2D object (typed FeaturePython)
  Area = 1.13097
  FirstAngle = 0
  LastAngle = 0
  MakeFace = true
  Placement = pos=(235.734,-139.471,0) rot=(0,0,1;3.56239rad)
  Radius = 0.6
FEATURE [Part::Part2DObjectPython] Rectangle081  # Draft 2D object (typed FeaturePython)
  Area = 0
  ChamferSize = 0
  Columns = 1
  FilletRadius = 0
  Height = 6
  Length = 6
  MakeFace = false
  Placement = pos=(247.354,-120.283,0) rot=(0,0,1;3.69294rad)
  Rows = 1
FEATURE [Part::Part2DObjectPython] Line081  # Draft 2D object (typed FeaturePython)
  Area = 0
  ChamferSize = 0
  Closed = false
  End = (195.261,-155.84,0)
  FilletRadius = 0
  Length = 60
  MakeFace = true
  Placement = pos=(521.403,-101.327,0) rot=(0,0,1;3.69294rad)
  Points = (2) [(246.37,-124.41,0),(306.37,-124.41,0)]
  Start = (246.37,-124.41,0)
  Subdivisions = 0
FEATURE [Part::Part2DObjectPython] Circle081  # Draft 2D object (typed FeaturePython)
  Area = 1.13097
  FirstAngle = 0
  LastAngle = 0
  MakeFace = true
  Placement = pos=(243.303,-126.296,0) rot=(0,0,1;3.69294rad)
  Radius = 0.6
FEATURE [Part::Part2DObjectPython] Rectangle082  # Draft 2D object (typed FeaturePython)
  Area = 0
  ChamferSize = 0
  Columns = 1
  FilletRadius = 0
  Height = 6
  Length = 6
  MakeFace = false
  Placement = pos=(253.39,-106.2,0) rot=(0,0,1;3.82314rad)
  Rows = 1
FEATURE [Part::Part2DObjectPython] Line082  # Draft 2D object (typed FeaturePython)
  Area = 0
  ChamferSize = 0
  Closed = false
  End = (206.354,-148.22,0)
  FilletRadius = 0
  Length = 60
  MakeFace = true
  Placement = pos=(518.954,-36.8137,0) rot=(0,0,1;3.82314rad)
  Points = (2) [(252.95,-110.42,0),(312.95,-110.42,0)]
  Start = (252.95,-110.42,0)
  Subdivisions = 0
FEATURE [Part::Part2DObjectPython] Circle082  # Draft 2D object (typed FeaturePython)
  Area = 1.13097
  FirstAngle = 0
  LastAngle = 0
  MakeFace = true
  Placement = pos=(250.154,-112.688,0) rot=(0,0,1;3.82314rad)
  Radius = 0.6
FEATURE [Part::Part2DObjectPython] Rectangle083  # Draft 2D object (typed FeaturePython)
  Area = 0
  ChamferSize = 0
  Columns = 1
  FilletRadius = 0
  Height = 6
  Length = 6
  MakeFace = false
  Placement = pos=(258.592,-91.8496,0) rot=(0,0,1;3.95963rad)
  Rows = 1
FEATURE [Part::Part2DObjectPython] Line083  # Draft 2D object (typed FeaturePython)
  Area = 0
  ChamferSize = 0
  Closed = false
  End = (217.711,-139.878,0)
  FilletRadius = 0
  Length = 60
  MakeFace = true
  Placement = pos=(505.739,27.0398,0) rot=(0,0,1;3.95963rad)
  Points = (2) [(258.73,-96.09,0),(318.73,-96.09,0)]
  Start = (258.73,-96.09,0)
  Subdivisions = 0
FEATURE [Part::Part2DObjectPython] Circle083  # Draft 2D object (typed FeaturePython)
  Area = 1.13097
  FirstAngle = 0
  LastAngle = 0
  MakeFace = true
  Placement = pos=(256.269,-98.7173,0) rot=(0,0,1;3.95963rad)
  Radius = 0.6
FEATURE [App::DocumentObjectGroup] Everything
  Group = -> [Rectangle,Line,Circle,Rectangle001,Line001,Circle001,Rectangle002,Line002,Circle002,Rectangle003,Line003,Circle003,Rectangle004,Line004,Circle004,Rectangle005,Line005,Circle005,Rectangle006,Line006,Circle006,Rectangle007,Line007,Circle007,Rectangle008,Line008,Circle008,Rectangle009,Line009,Circle009,Rectangle010,Line010,Circle010,Rectangle011,Line011,Circle011,Rectangle012,Line012,Circle012,+213 more]
